# Revit family: 0010232
name_source: partatom
category: Lighting Fixtures
revit_build: Autodesk Revit 2017 (Build: 20190507_1515(x64)
units: mm (PartAtom-declared; Revit-internal decimal feet)

## family parameters
Cut with Voids When Loaded = No
Host = Face
Light Source = Yes
OmniClass Number = 23.80.70.00
OmniClass Title = Lighting
Part Type = Normal
Room Calculation Point = No
Round Connector Dimension = Use Diameter
Shared = No

## types (60) — shared parameters
Assembly Code = D5020200
AssetType = Fixed
BODY_SYL = 36 mm  [stored 0.11811 ft]
BRACKET_HEIGHT_SYL = 9 mm
CHAMFER_SYL = 19 mm
ClassificationName = Uniclass2015
ClassificationValue = EF_70_80
Color Filter = 16777215
DIF_HEIGHT_SYL = 24 mm
DIF_WIDHT_SYL = 35 mm  [stored 0.114829 ft]
Default Elevation = 1219 mm
Dimming Lamp Color Temperature Shift = <None>
DocumentationLiterature = http://www.sylvania-lighting.com
ElectricShockClassification = Class I
Emit Shape Visible in Rendering = No
Emit from Circle Diameter = 610 mm
IfcExportAs = IfcLightFixtureType
IfcExportType = IfcLightFixtureType
ImpactProtectionIndex = IK08
IngressProtection = IP66
Keynote = 16500
LEGHT_1200-_SYL = -600 mm
LEGHT_1200_SYL = 600 mm
LEGHT_1500-_SYL = -750 mm  [stored -2.46063 ft]
LEGHT_1500_SYL = 750 mm  [stored 2.46063 ft]
LEGHT_650-_SYL = -325 mm  [stored -1.06627 ft]
LENGHT_650_SYL = 325 mm  [stored 1.06627 ft]
Lamp = LED
LampColourRenderingIndex = 80
LampsType = LED
MID_WIDTH_SYL = 36 mm  [stored 0.11811 ft]
Manufacturer = Feilo Sylvania
ManufacturerName = Feilo Sylvania
Material = pc polycarbonate housing, pc polycarbonate diffuser
Material_1_SYL = Default
Material_2_SYL = <By Category>
Material_3_SYL = <By Category>
Material_4_SYL = <By Category>
NominalDepth = 87 mm  [stored 0.285433 ft]
NominalHeight = 80 mm  [stored 0.262467 ft]
TOP_WIDTH_SYL = 34 mm
Tilt Angle = -90.00°
Type Image = <None>
URL = http://www.sylvania-lighting.com
Voltage = 0 V
WIDTH_SYL = 45 mm
zero-valued in all types: Cost

## per-type parameters (varying)
- 0010278 RESISTO 1500 HE IP66 8300LM 840: Apparent Load=54 VA; BRACKET_DIST_SYL=594 mm; BRACKET_WIDTH_SYL=550 mm; Description=Resisto, integrated LED weatherproof luminaire, with UV stabilized flat diffuser designed to achieve uniform lit appearance, optimise light output and to reduce glare. 301 stainless steel diffuser clips and fixing brackets for surface mounting. Polycarbonate housing and diffuser - no yellow discolouration over time. 8300lm; 54W; 154lm/W; 4000K; SDCM<3; non dimmable; CRI80; IP66; IK08; Class I; 69,000hrs (L80B20) lifespan; 1500mm x 89mm x 88mm; D-mark.; L0650_SYL=No; L1200_SYL=No; L1500_SYL=Yes; LENGHT-_CHAMFER_SYL=-750 mm  [stored -2.46063 ft]; LENGHT-_SYL=-742 mm  [stored -2.43438 ft]; LENGHT_CHAMFER_SYL=750 mm  [stored 2.46063 ft]; LENGHT_SYL=742 mm  [stored 2.43438 ft]; LampColourTemperature=4000 K; LampMacAdamStep=3; LampNominalLuminous=8300 lm; LuminousEfficacy=154 lm/W; Model=Resisto 1500 HE IP66 8300lm 840; ModelNumber=0010278; ModelReference=Resisto 1500 HE IP66 8300lm 840; Name=Resisto 1500 HE IP66 8300lm 840; NominalLength=1500 mm  [stored 4.92126 ft]; Photometric Web File=0010278.ies; PowerConsumption=54 W; PowerFactor=0.95; TypeName=Resisto 1500 HE IP66 8300lm 840; Weight=1.95 kg
- 0010274 RESISTO 1500 HE IP66 DALI 7100LM 840: Apparent Load=46 VA; BRACKET_DIST_SYL=594 mm; BRACKET_WIDTH_SYL=550 mm; Description=Resisto, integrated LED weatherproof luminaire, with UV stabilized flat diffuser designed to achieve uniform lit appearance, optimise light output and to reduce glare. 301 stainless steel diffuser clips and fixing brackets for surface mounting. Polycarbonate housing and diffuser - no yellow discolouration over time. 7100lm; 46W; 154lm/W; 4000K; SDCM<3; DALI dimmable; CRI80; IP66; IK08; Class I; 69,000hrs (L80B20) lifespan; 1500mm x 89mm x 88mm; D-mark.; L0650_SYL=No; L1200_SYL=No; L1500_SYL=Yes; LENGHT-_CHAMFER_SYL=-750 mm  [stored -2.46063 ft]; LENGHT-_SYL=-742 mm  [stored -2.43438 ft]; LENGHT_CHAMFER_SYL=750 mm  [stored 2.46063 ft]; LENGHT_SYL=742 mm  [stored 2.43438 ft]; LampColourTemperature=4000 K; LampMacAdamStep=3; LampNominalLuminous=7100 lm; LuminousEfficacy=154 lm/W; Model=Resisto 1500 HE IP66 DALI 7100lm 840; ModelNumber=0010274; ModelReference=Resisto 1500 HE IP66 DALI 7100lm 840; Name=Resisto 1500 HE IP66 DALI 7100lm 840; NominalLength=1500 mm  [stored 4.92126 ft]; Photometric Web File=0010274.ies; PowerConsumption=46 W; PowerFactor=0.98; TypeName=Resisto 1500 HE IP66 DALI 7100lm 840; Weight=2.01 kg
- 0010273 RESISTO 1500 HE IP66 DALI 4000LM 840: Apparent Load=25 VA; BRACKET_DIST_SYL=594 mm; BRACKET_WIDTH_SYL=550 mm; Description=Resisto, integrated LED weatherproof luminaire, with UV stabilized flat diffuser designed to achieve uniform lit appearance, optimise light output and to reduce glare. 301 stainless steel diffuser clips and fixing brackets for surface mounting. Polycarbonate housing and diffuser - no yellow discolouration over time. 4000lm; 25W; 160lm/W; 4000K; SDCM<3; DALI dimmable; CRI80; IP66; IK08; Class I; 69,000hrs (L80B20) lifespan; 1500mm x 89mm x 88mm; D-mark.; L0650_SYL=No; L1200_SYL=No; L1500_SYL=Yes; LENGHT-_CHAMFER_SYL=-750 mm  [stored -2.46063 ft]; LENGHT-_SYL=-742 mm  [stored -2.43438 ft]; LENGHT_CHAMFER_SYL=750 mm  [stored 2.46063 ft]; LENGHT_SYL=742 mm  [stored 2.43438 ft]; LampColourTemperature=4000 K; LampMacAdamStep=3; LampNominalLuminous=4000 lm; LuminousEfficacy=160 lm/W; Model=Resisto 1500 HE IP66 DALI 4000lm 840; ModelNumber=0010273; ModelReference=Resisto 1500 HE IP66 DALI 4000lm 840; Name=Resisto 1500 HE IP66 DALI 4000lm 840; NominalLength=1500 mm  [stored 4.92126 ft]; Photometric Web File=0010273.ies; PowerConsumption=25 W; PowerFactor=0.98; TypeName=Resisto 1500 HE IP66 DALI 4000lm 840; Weight=1.95 kg
- 0010272 RESISTO 1500 HE IP66 7100LM 840 EM: Apparent Load=50 VA; BRACKET_DIST_SYL=594 mm; BRACKET_WIDTH_SYL=550 mm; Description=Resisto, integrated LED weatherproof luminaire, with UV stabilized flat diffuser designed to achieve uniform lit appearance, optimise light output and to reduce glare. 301 stainless steel diffuser clips and fixing brackets for surface mounting. Polycarbonate housing and diffuser - no yellow discolouration over time. 7100lm; 50W; 142lm/W; 4000K; SDCM<3; non dimmable; CRI80; IP66; IK08; Class I; 69,000hrs (L80B20) lifespan; 1500mm x 89mm x 88mm; D-mark; 3-hour maintained emergency batteries.; L0650_SYL=No; L1200_SYL=No; L1500_SYL=Yes; LENGHT-_CHAMFER_SYL=-750 mm  [stored -2.46063 ft]; LENGHT-_SYL=-742 mm  [stored -2.43438 ft]; LENGHT_CHAMFER_SYL=750 mm  [stored 2.46063 ft]; LENGHT_SYL=742 mm  [stored 2.43438 ft]; LampColourTemperature=4000 K; LampMacAdamStep=3; LampNominalLuminous=7100 lm; LuminousEfficacy=142 lm/W; Model=Resisto 1500 HE IP66 7100lm 840 EM; ModelNumber=0010272; ModelReference=Resisto 1500 HE IP66 7100lm 840 EM; Name=Resisto 1500 HE IP66 7100lm 840 EM; NominalLength=1500 mm  [stored 4.92126 ft]; Photometric Web File=0010272.ies; PowerConsumption=50 W; PowerFactor=0.95; TypeName=Resisto 1500 HE IP66 7100lm 840 EM; Weight=2.58 kg
- 0010271 RESISTO 1500 HE IP66 4000LM 840 EM: Apparent Load=29 VA; BRACKET_DIST_SYL=594 mm; BRACKET_WIDTH_SYL=550 mm; Description=Resisto, integrated LED weatherproof luminaire, with UV stabilized flat diffuser designed to achieve uniform lit appearance, optimise light output and to reduce glare. 301 stainless steel diffuser clips and fixing brackets for surface mounting. Polycarbonate housing and diffuser - no yellow discolouration over time. 4000lm; 29W; 138lm/W; 4000K; SDCM<3; non dimmable; CRI80; IP66; IK08; Class I; 69,000hrs (L80B20) lifespan; 1500mm x 89mm x 88mm; D-mark; 3-hour maintained emergency batteries.; L0650_SYL=No; L1200_SYL=No; L1500_SYL=Yes; LENGHT-_CHAMFER_SYL=-750 mm  [stored -2.46063 ft]; LENGHT-_SYL=-742 mm  [stored -2.43438 ft]; LENGHT_CHAMFER_SYL=750 mm  [stored 2.46063 ft]; LENGHT_SYL=742 mm  [stored 2.43438 ft]; LampColourTemperature=4000 K; LampMacAdamStep=3; LampNominalLuminous=4000 lm; LuminousEfficacy=138 lm/W; Model=Resisto 1500 HE IP66 4000lm 840 EM; ModelNumber=0010271; ModelReference=Resisto 1500 HE IP66 4000lm 840 EM; Name=Resisto 1500 HE IP66 4000lm 840 EM; NominalLength=1500 mm  [stored 4.92126 ft]; Photometric Web File=0010271.ies; PowerConsumption=29 W; PowerFactor=0.95; TypeName=Resisto 1500 HE IP66 4000lm 840 EM; Weight=2.51 kg
- 0010269 RESISTO 1500 HE IP66 7100LM 840: Apparent Load=46 VA; BRACKET_DIST_SYL=594 mm; BRACKET_WIDTH_SYL=550 mm; Description=Resisto, integrated LED weatherproof luminaire, with UV stabilized flat diffuser designed to achieve uniform lit appearance, optimise light output and to reduce glare. 301 stainless steel diffuser clips and fixing brackets for surface mounting. Polycarbonate housing and diffuser - no yellow discolouration over time. 7100lm; 46W; 154lm/W; 4000K; SDCM<3; non dimmable; CRI80; IP66; IK08; Class I; 69,000hrs (L80B20) lifespan; 1500mm x 89mm x 88mm; D-mark.; L0650_SYL=No; L1200_SYL=No; L1500_SYL=Yes; LENGHT-_CHAMFER_SYL=-750 mm  [stored -2.46063 ft]; LENGHT-_SYL=-742 mm  [stored -2.43438 ft]; LENGHT_CHAMFER_SYL=750 mm  [stored 2.46063 ft]; LENGHT_SYL=742 mm  [stored 2.43438 ft]; LampColourTemperature=4000 K; LampMacAdamStep=3; LampNominalLuminous=7100 lm; LuminousEfficacy=154 lm/W; Model=Resisto  1500 HE IP66 7100lm 840; ModelNumber=0010269; ModelReference=Resisto  1500 HE IP66 7100lm 840; Name=Resisto  1500 HE IP66 7100lm 840; NominalLength=1500 mm  [stored 4.92126 ft]; Photometric Web File=0010269.ies; PowerConsumption=46 W; PowerFactor=0.95; TypeName=Resisto  1500 HE IP66 7100lm 840; Weight=1.95 kg
- 0010268 RESISTO 1500 HE IP66 4000LM 840: Apparent Load=25 VA; BRACKET_DIST_SYL=594 mm; BRACKET_WIDTH_SYL=550 mm; Description=Resisto, integrated LED weatherproof luminaire, with UV stabilized flat diffuser designed to achieve uniform lit appearance, optimise light output and to reduce glare. 301 stainless steel diffuser clips and fixing brackets for surface mounting. Polycarbonate housing and diffuser - no yellow discolouration over time. 4000lm; 25W; 160lm/W; 4000K; SDCM<3; non dimmable; CRI80; IP66; IK08; Class I; 69,000hrs (L80B20) lifespan; 1500mm x 89mm x 88mm; D-mark.; L0650_SYL=No; L1200_SYL=No; L1500_SYL=Yes; LENGHT-_CHAMFER_SYL=-750 mm  [stored -2.46063 ft]; LENGHT-_SYL=-742 mm  [stored -2.43438 ft]; LENGHT_CHAMFER_SYL=750 mm  [stored 2.46063 ft]; LENGHT_SYL=742 mm  [stored 2.43438 ft]; LampColourTemperature=4000 K; LampMacAdamStep=3; LampNominalLuminous=4000 lm; LuminousEfficacy=160 lm/W; Model=Resisto  1500 HE IP66 4000lm 840; ModelNumber=0010268; ModelReference=Resisto  1500 HE IP66 4000lm 840; Name=Resisto  1500 HE IP66 4000lm 840; NominalLength=1500 mm  [stored 4.92126 ft]; Photometric Web File=0010268.ies; PowerConsumption=25 W; PowerFactor=0.95; TypeName=Resisto  1500 HE IP66 4000lm 840; Weight=1.87 kg
- 0010261 RESISTO 1500 IP66 DALI 8300LM 840: Apparent Load=61 VA; BRACKET_DIST_SYL=594 mm; BRACKET_WIDTH_SYL=550 mm; Description=Resisto, integrated LED weatherproof luminaire, with UV stabilized flat diffuser designed to achieve uniform lit appearance, optimise light output and to reduce glare. 301 stainless steel diffuser clips and fixing brackets for surface mounting. Polycarbonate housing and diffuser - no yellow discolouration over time. 8300lm; 61W; 136lm/W; 4000K; SDCM<5; DALI dimmable; CRI80; IP66; IK08; Class I; 69,000hrs (L80B20) lifespan; 1500mm x 89mm x 88mm; D-mark.; L0650_SYL=No; L1200_SYL=No; L1500_SYL=Yes; LENGHT-_CHAMFER_SYL=-750 mm  [stored -2.46063 ft]; LENGHT-_SYL=-742 mm  [stored -2.43438 ft]; LENGHT_CHAMFER_SYL=750 mm  [stored 2.46063 ft]; LENGHT_SYL=742 mm  [stored 2.43438 ft]; LampColourTemperature=4000 K; LampMacAdamStep=5; LampNominalLuminous=8300 lm; LuminousEfficacy=136 lm/W; Model=Resisto  1500 IP66 DALI 8300lm 840; ModelNumber=0010261; ModelReference=Resisto  1500 IP66 DALI 8300lm 840; Name=Resisto  1500 IP66 DALI 8300lm 840; NominalLength=1500 mm  [stored 4.92126 ft]; Photometric Web File=0010261.ies; PowerConsumption=61 W; PowerFactor=0.99; TypeName=Resisto  1500 IP66 DALI 8300lm 840; Weight=2.01 kg
- 0010260 RESISTO 1500 IP66 DALI 7100LM 840: Apparent Load=52 VA; BRACKET_DIST_SYL=594 mm; BRACKET_WIDTH_SYL=550 mm; Description=Resisto, integrated LED weatherproof luminaire, with UV stabilized flat diffuser designed to achieve uniform lit appearance, optimise light output and to reduce glare. 301 stainless steel diffuser clips and fixing brackets for surface mounting. Polycarbonate housing and diffuser - no yellow discolouration over time. 7100lm; 52W; 137lm/W; 4000K; SDCM<5; DALI dimmable; CRI80; IP66; IK08; Class I; 69,000hrs (L80B20) lifespan; 1500mm x 89mm x 88mm; D-mark.; L0650_SYL=No; L1200_SYL=No; L1500_SYL=Yes; LENGHT-_CHAMFER_SYL=-750 mm  [stored -2.46063 ft]; LENGHT-_SYL=-742 mm  [stored -2.43438 ft]; LENGHT_CHAMFER_SYL=750 mm  [stored 2.46063 ft]; LENGHT_SYL=742 mm  [stored 2.43438 ft]; LampColourTemperature=4000 K; LampMacAdamStep=5; LampNominalLuminous=7100 lm; LuminousEfficacy=137 lm/W; Model=Resisto  1500 IP66 DALI 7100lm 840; ModelNumber=0010260; ModelReference=Resisto  1500 IP66 DALI 7100lm 840; Name=Resisto  1500 IP66 DALI 7100lm 840; NominalLength=1500 mm  [stored 4.92126 ft]; Photometric Web File=0010260.ies; PowerConsumption=52 W; PowerFactor=0.99; TypeName=Resisto  1500 IP66 DALI 7100lm 840; Weight=2.01 kg
- 0010259 RESISTO 1500 IP66 DALI 4000LM 840: Apparent Load=30 VA; BRACKET_DIST_SYL=594 mm; BRACKET_WIDTH_SYL=550 mm; Description=Resisto, integrated LED weatherproof luminaire, with UV stabilized flat diffuser designed to achieve uniform lit appearance, optimise light output and to reduce glare. 301 stainless steel diffuser clips and fixing brackets for surface mounting. Polycarbonate housing and diffuser - no yellow discolouration over time. 4000lm; 30W; 133lm/W; 4000K; SDCM<5; DALI dimmable; CRI80; IP66; IK08; Class I; 69,000hrs (L80B20) lifespan; 1500mm x 89mm x 88mm; D-mark.; L0650_SYL=No; L1200_SYL=No; L1500_SYL=Yes; LENGHT-_CHAMFER_SYL=-750 mm  [stored -2.46063 ft]; LENGHT-_SYL=-742 mm  [stored -2.43438 ft]; LENGHT_CHAMFER_SYL=750 mm  [stored 2.46063 ft]; LENGHT_SYL=742 mm  [stored 2.43438 ft]; LampColourTemperature=4000 K; LampMacAdamStep=5; LampNominalLuminous=4000 lm; LuminousEfficacy=133 lm/W; Model=Resisto  1500 IP66 DALI 4000lm 840; ModelNumber=0010259; ModelReference=Resisto  1500 IP66 DALI 4000lm 840; Name=Resisto  1500 IP66 DALI 4000lm 840; NominalLength=1500 mm  [stored 4.92126 ft]; Photometric Web File=0010259.ies; PowerConsumption=30 W; PowerFactor=0.98; TypeName=Resisto  1500 IP66 DALI 4000lm 840; Weight=1.95 kg
- 0010258 RESISTO 1500 IP66 MWCOR 7100LM 840: Apparent Load=52 VA; BRACKET_DIST_SYL=594 mm; BRACKET_WIDTH_SYL=550 mm; Description=Resisto, integrated LED weatherproof luminaire, with UV stabilized flat diffuser designed to achieve uniform lit appearance, optimise light output and to reduce glare. 301 stainless steel diffuser clips and fixing brackets for surface mounting. Polycarbonate housing and diffuser - no yellow discolouration over time. 7100lm; 52W; 137lm/W; 4000K; SDCM<5; non dimmable; CRI80; IP66; IK08; Class I; 69,000hrs (L80B20) lifespan; 1500mm x 89mm x 88mm; D-mark; corridor function with microwave presence sensor.; L0650_SYL=No; L1200_SYL=No; L1500_SYL=Yes; LENGHT-_CHAMFER_SYL=-750 mm  [stored -2.46063 ft]; LENGHT-_SYL=-742 mm  [stored -2.43438 ft]; LENGHT_CHAMFER_SYL=750 mm  [stored 2.46063 ft]; LENGHT_SYL=742 mm  [stored 2.43438 ft]; LampColourTemperature=4000 K; LampMacAdamStep=5; LampNominalLuminous=7100 lm; LuminousEfficacy=137 lm/W; Model=Resisto  1500 IP66 MWcor 7100lm 840; ModelNumber=0010258; ModelReference=Resisto  1500 IP66 MWcor 7100lm 840; Name=Resisto  1500 IP66 MWcor 7100lm 840; NominalLength=1500 mm  [stored 4.92126 ft]; Photometric Web File=0010258.ies; PowerConsumption=52 W; PowerFactor=0.99; TypeName=Resisto  1500 IP66 MWcor 7100lm 840; Weight=2.06 kg
- 0010257 RESISTO 1500 IP66 MWCOR 4000LM 840: Apparent Load=30 VA; BRACKET_DIST_SYL=594 mm; BRACKET_WIDTH_SYL=550 mm; Description=Resisto, integrated LED weatherproof luminaire, with UV stabilized flat diffuser designed to achieve uniform lit appearance, optimise light output and to reduce glare. 301 stainless steel diffuser clips and fixing brackets for surface mounting. Polycarbonate housing and diffuser - no yellow discolouration over time. 4000lm; 30W; 133lm/W; 4000K; SDCM<5; non dimmable; CRI80; IP66; IK08; Class I; 69,000hrs (L80B20) lifespan; 1500mm x 89mm x 88mm; D-mark; corridor function with microwave presence sensor.; L0650_SYL=No; L1200_SYL=No; L1500_SYL=Yes; LENGHT-_CHAMFER_SYL=-750 mm  [stored -2.46063 ft]; LENGHT-_SYL=-742 mm  [stored -2.43438 ft]; LENGHT_CHAMFER_SYL=750 mm  [stored 2.46063 ft]; LENGHT_SYL=742 mm  [stored 2.43438 ft]; LampColourTemperature=4000 K; LampMacAdamStep=5; LampNominalLuminous=4000 lm; LuminousEfficacy=133 lm/W; Model=Resisto  1500 IP66 MWcor 4000lm 840; ModelNumber=0010257; ModelReference=Resisto  1500 IP66 MWcor 4000lm 840; Name=Resisto  1500 IP66 MWcor 4000lm 840; NominalLength=1500 mm  [stored 4.92126 ft]; Photometric Web File=0010257.ies; PowerConsumption=30 W; PowerFactor=0.98; TypeName=Resisto  1500 IP66 MWcor 4000lm 840; Weight=2.0 kg
- 0010256 RESISTO 1500 IP66 MW 7100LM 840: Apparent Load=52 VA; BRACKET_DIST_SYL=594 mm; BRACKET_WIDTH_SYL=550 mm; Description=Resisto, integrated LED weatherproof luminaire, with UV stabilized flat diffuser designed to achieve uniform lit appearance, optimise light output and to reduce glare. 301 stainless steel diffuser clips and fixing brackets for surface mounting. Polycarbonate housing and diffuser - no yellow discolouration over time. 7100lm; 52W; 137lm/W; 4000K; SDCM<5; non dimmable; CRI80; IP66; IK08; Class I; 69,000hrs (L80B20) lifespan; 1500mm x 89mm x 88mm; D-mark; MW On/Off.; L0650_SYL=No; L1200_SYL=No; L1500_SYL=Yes; LENGHT-_CHAMFER_SYL=-750 mm  [stored -2.46063 ft]; LENGHT-_SYL=-742 mm  [stored -2.43438 ft]; LENGHT_CHAMFER_SYL=750 mm  [stored 2.46063 ft]; LENGHT_SYL=742 mm  [stored 2.43438 ft]; LampColourTemperature=4000 K; LampMacAdamStep=5; LampNominalLuminous=7100 lm; LuminousEfficacy=137 lm/W; Model=Resisto  1500 IP66 MW 7100lm 840; ModelNumber=0010256; ModelReference=Resisto  1500 IP66 MW 7100lm 840; Name=Resisto  1500 IP66 MW 7100lm 840; NominalLength=1500 mm  [stored 4.92126 ft]; Photometric Web File=0010256.ies; PowerConsumption=52 W; PowerFactor=0.95; TypeName=Resisto  1500 IP66 MW 7100lm 840; Weight=2.0 kg
- 0010255 RESISTO 1500 IP66 MW 4000LM 840: Apparent Load=30 VA; BRACKET_DIST_SYL=594 mm; BRACKET_WIDTH_SYL=550 mm; Description=Resisto, integrated LED weatherproof luminaire, with UV stabilized flat diffuser designed to achieve uniform lit appearance, optimise light output and to reduce glare. 301 stainless steel diffuser clips and fixing brackets for surface mounting. Polycarbonate housing and diffuser - no yellow discolouration over time. 4000lm; 30W; 133lm/W; 4000K; SDCM<5; non dimmable; CRI80; IP66; IK08; Class I; 69,000hrs (L80B20) lifespan; 1500mm x 89mm x 88mm; D-mark; MW On/Off.; L0650_SYL=No; L1200_SYL=No; L1500_SYL=Yes; LENGHT-_CHAMFER_SYL=-750 mm  [stored -2.46063 ft]; LENGHT-_SYL=-742 mm  [stored -2.43438 ft]; LENGHT_CHAMFER_SYL=750 mm  [stored 2.46063 ft]; LENGHT_SYL=742 mm  [stored 2.43438 ft]; LampColourTemperature=4000 K; LampMacAdamStep=5; LampNominalLuminous=4000 lm; LuminousEfficacy=133 lm/W; Model=Resisto  1500 IP66 MW 4000lm 840; ModelNumber=0010255; ModelReference=Resisto  1500 IP66 MW 4000lm 840; Name=Resisto  1500 IP66 MW 4000lm 840; NominalLength=1500 mm  [stored 4.92126 ft]; Photometric Web File=0010255.ies; PowerConsumption=30 W; PowerFactor=0.95; TypeName=Resisto  1500 IP66 MW 4000lm 840; Weight=1.92 kg
- 0010254 RESISTO 1500 IP66 7100LM 840 EM: Apparent Load=56 VA; BRACKET_DIST_SYL=594 mm; BRACKET_WIDTH_SYL=550 mm; Description=Resisto, integrated LED weatherproof luminaire, with UV stabilized flat diffuser designed to achieve uniform lit appearance, optimise light output and to reduce glare. 301 stainless steel diffuser clips and fixing brackets for surface mounting. Polycarbonate housing and diffuser - no yellow discolouration over time. 7100lm; 56W; 127lm/W; 4000K; SDCM<5; non dimmable; CRI80; IP66; IK08; Class I; 69,000hrs (L80B20) lifespan; 1500mm x 89mm x 88mm; D-mark; 3-hour maintained emergency batteries.; L0650_SYL=No; L1200_SYL=No; L1500_SYL=Yes; LENGHT-_CHAMFER_SYL=-750 mm  [stored -2.46063 ft]; LENGHT-_SYL=-742 mm  [stored -2.43438 ft]; LENGHT_CHAMFER_SYL=750 mm  [stored 2.46063 ft]; LENGHT_SYL=742 mm  [stored 2.43438 ft]; LampColourTemperature=4000 K; LampMacAdamStep=5; LampNominalLuminous=7100 lm; LuminousEfficacy=127 lm/W; Model=Resisto  1500 IP66 7100lm 840 EM; ModelNumber=0010254; ModelReference=Resisto  1500 IP66 7100lm 840 EM; Name=Resisto  1500 IP66 7100lm 840 EM; NominalLength=1500 mm  [stored 4.92126 ft]; Photometric Web File=0010254.ies; PowerConsumption=56 W; PowerFactor=0.95; TypeName=Resisto  1500 IP66 7100lm 840 EM; Weight=2.59 kg
- 0010253 RESISTO 1500 IP66 4000LM 840 EM: Apparent Load=34 VA; BRACKET_DIST_SYL=594 mm; BRACKET_WIDTH_SYL=550 mm; Description=Resisto, integrated LED weatherproof luminaire, with UV stabilized flat diffuser designed to achieve uniform lit appearance, optimise light output and to reduce glare. 301 stainless steel diffuser clips and fixing brackets for surface mounting. Polycarbonate housing and diffuser - no yellow discolouration over time. 4000lm; 34W; 118lm/W; 4000K; SDCM<5; non dimmable; CRI80; IP66; IK08; Class I; 69,000hrs (L80B20) lifespan; 1500mm x 89mm x 88mm; D-mark; 3-hour maintained emergency batteries.; L0650_SYL=No; L1200_SYL=No; L1500_SYL=Yes; LENGHT-_CHAMFER_SYL=-750 mm  [stored -2.46063 ft]; LENGHT-_SYL=-742 mm  [stored -2.43438 ft]; LENGHT_CHAMFER_SYL=750 mm  [stored 2.46063 ft]; LENGHT_SYL=742 mm  [stored 2.43438 ft]; LampColourTemperature=4000 K; LampMacAdamStep=5; LampNominalLuminous=4000 lm; LuminousEfficacy=118 lm/W; Model=Resisto  1500 IP66 4000lm 840 EM; ModelNumber=0010253; ModelReference=Resisto  1500 IP66 4000lm 840 EM; Name=Resisto  1500 IP66 4000lm 840 EM; NominalLength=1500 mm  [stored 4.92126 ft]; Photometric Web File=0010253.ies; PowerConsumption=34 W; PowerFactor=0.95; TypeName=Resisto  1500 IP66 4000lm 840 EM; Weight=2.5 kg
- 0010252 RESISTO 1500 IP66 7100LM 840 5XTH: Apparent Load=52 VA; BRACKET_DIST_SYL=594 mm; BRACKET_WIDTH_SYL=550 mm; Description=Resisto, integrated LED weatherproof luminaire, with UV stabilized flat diffuser designed to achieve uniform lit appearance, optimise light output and to reduce glare. 301 stainless steel diffuser clips and fixing brackets for surface mounting. Polycarbonate housing and diffuser - no yellow discolouration over time. 7100lm; 52W; 137lm/W; 4000K; SDCM<5; non dimmable; CRI80; IP66; IK08; Class I; 69,000hrs (L80B20) lifespan; 1500mm x 89mm x 88mm; D-mark; through wiring.; L0650_SYL=No; L1200_SYL=No; L1500_SYL=Yes; LENGHT-_CHAMFER_SYL=-750 mm  [stored -2.46063 ft]; LENGHT-_SYL=-742 mm  [stored -2.43438 ft]; LENGHT_CHAMFER_SYL=750 mm  [stored 2.46063 ft]; LENGHT_SYL=742 mm  [stored 2.43438 ft]; LampColourTemperature=4000 K; LampMacAdamStep=5; LampNominalLuminous=7100 lm; LuminousEfficacy=137 lm/W; Model=Resisto 1500 IP66 7100lm 840 5xTH; ModelNumber=0010252; ModelReference=Resisto 1500 IP66 7100lm 840 5xTH; Name=Resisto 1500 IP66 7100lm 840 5xTH; NominalLength=1500 mm  [stored 4.92126 ft]; Photometric Web File=0010252.ies; PowerConsumption=52 W; PowerFactor=0.95; TypeName=Resisto 1500 IP66 7100lm 840 5xTH; Weight=2.18 kg
- 0010251 RESISTO 1500 IP66 4000LM 840 5XTH: Apparent Load=30 VA; BRACKET_DIST_SYL=594 mm; BRACKET_WIDTH_SYL=550 mm; Description=Resisto, integrated LED weatherproof luminaire, with UV stabilized flat diffuser designed to achieve uniform lit appearance, optimise light output and to reduce glare. 301 stainless steel diffuser clips and fixing brackets for surface mounting. Polycarbonate housing and diffuser - no yellow discolouration over time. 4000lm; 30W; 133lm/W; 4000K; SDCM<5; non dimmable; CRI80; IP66; IK08; Class I; 69,000hrs (L80B20) lifespan; 1500mm x 89mm x 88mm; D-mark; through wiring.; L0650_SYL=No; L1200_SYL=No; L1500_SYL=Yes; LENGHT-_CHAMFER_SYL=-750 mm  [stored -2.46063 ft]; LENGHT-_SYL=-742 mm  [stored -2.43438 ft]; LENGHT_CHAMFER_SYL=750 mm  [stored 2.46063 ft]; LENGHT_SYL=742 mm  [stored 2.43438 ft]; LampColourTemperature=4000 K; LampMacAdamStep=5; LampNominalLuminous=4000 lm; LuminousEfficacy=133 lm/W; Model=Resisto 1500 IP66 4000lm 840 5xTH; ModelNumber=0010251; ModelReference=Resisto 1500 IP66 4000lm 840 5xTH; Name=Resisto 1500 IP66 4000lm 840 5xTH; NominalLength=1500 mm  [stored 4.92126 ft]; Photometric Web File=0010251.ies; PowerConsumption=30 W; PowerFactor=0.95; TypeName=Resisto 1500 IP66 4000lm 840 5xTH; Weight=2.1 kg
- 0010250 RESISTO 1500 IP66 7100LM 840 QC: Apparent Load=52 VA; BRACKET_DIST_SYL=594 mm; BRACKET_WIDTH_SYL=550 mm; Description=Resisto, integrated LED weatherproof luminaire, with UV stabilized flat diffuser designed to achieve uniform lit appearance, optimise light output and to reduce glare. 301 stainless steel diffuser clips and fixing brackets for surface mounting. Polycarbonate housing and diffuser - no yellow discolouration over time. 7100lm; 52W; 137lm/W; 4000K; SDCM<5; non dimmable; CRI80; IP66; IK08; Class I; 69,000hrs (L80B20) lifespan; 1500mm x 89mm x 88mm; D-mark; assembled with quick connector.; L0650_SYL=No; L1200_SYL=No; L1500_SYL=Yes; LENGHT-_CHAMFER_SYL=-750 mm  [stored -2.46063 ft]; LENGHT-_SYL=-742 mm  [stored -2.43438 ft]; LENGHT_CHAMFER_SYL=750 mm  [stored 2.46063 ft]; LENGHT_SYL=742 mm  [stored 2.43438 ft]; LampColourTemperature=4000 K; LampMacAdamStep=5; LampNominalLuminous=7100 lm; LuminousEfficacy=137 lm/W; Model=Resisto  1500 IP66 7100lm 840 QC; ModelNumber=0010250; ModelReference=Resisto  1500 IP66 7100lm 840 QC; Name=Resisto  1500 IP66 7100lm 840 QC; NominalLength=1512 mm  [stored 4.96063 ft]; Photometric Web File=0010250.ies; PowerConsumption=52 W; PowerFactor=0.95; TypeName=Resisto  1500 IP66 7100lm 840 QC; Weight=2.02 kg
- 0010249 RESISTO 1500 IP66 4000LM 840 QC: Apparent Load=30 VA; BRACKET_DIST_SYL=594 mm; BRACKET_WIDTH_SYL=550 mm; Description=Resisto, integrated LED weatherproof luminaire, with UV stabilized flat diffuser designed to achieve uniform lit appearance, optimise light output and to reduce glare. 301 stainless steel diffuser clips and fixing brackets for surface mounting. Polycarbonate housing and diffuser - no yellow discolouration over time. 4000lm; 30W; 133lm/W; 4000K; SDCM<5; non dimmable; CRI80; IP66; IK08; Class I; 69,000hrs (L80B20) lifespan; 1500mm x 89mm x 88mm; D-mark; assembled with quick connector.; L0650_SYL=No; L1200_SYL=No; L1500_SYL=Yes; LENGHT-_CHAMFER_SYL=-750 mm  [stored -2.46063 ft]; LENGHT-_SYL=-742 mm  [stored -2.43438 ft]; LENGHT_CHAMFER_SYL=750 mm  [stored 2.46063 ft]; LENGHT_SYL=742 mm  [stored 2.43438 ft]; LampColourTemperature=4000 K; LampMacAdamStep=5; LampNominalLuminous=4000 lm; LuminousEfficacy=133 lm/W; Model=Resisto  1500 IP66 4000lm 840 QC; ModelNumber=0010249; ModelReference=Resisto  1500 IP66 4000lm 840 QC; Name=Resisto  1500 IP66 4000lm 840 QC; NominalLength=1512 mm  [stored 4.96063 ft]; Photometric Web File=0010249.ies; PowerConsumption=30 W; PowerFactor=0.95; TypeName=Resisto  1500 IP66 4000lm 840 QC; Weight=1.94 kg
- 0010248 RESISTO 1500 IP66 8300LM 865: Apparent Load=61 VA; BRACKET_DIST_SYL=594 mm; BRACKET_WIDTH_SYL=550 mm; Description=Resisto, integrated LED weatherproof luminaire, with UV stabilized flat diffuser designed to achieve uniform lit appearance, optimise light output and to reduce glare. 301 stainless steel diffuser clips and fixing brackets for surface mounting. Polycarbonate housing and diffuser - no yellow discolouration over time. 8300lm; 61W; 136lm/W; 6500K; SDCM<5; non dimmable; CRI80; IP66; IK08; Class I; 69,000hrs (L80B20) lifespan; 1500mm x 89mm x 88mm; D-mark.; L0650_SYL=No; L1200_SYL=No; L1500_SYL=Yes; LENGHT-_CHAMFER_SYL=-750 mm  [stored -2.46063 ft]; LENGHT-_SYL=-742 mm  [stored -2.43438 ft]; LENGHT_CHAMFER_SYL=750 mm  [stored 2.46063 ft]; LENGHT_SYL=742 mm  [stored 2.43438 ft]; LampColourTemperature=6500 K; LampMacAdamStep=5; LampNominalLuminous=8300 lm; LuminousEfficacy=136 lm/W; Model=Resisto  1500 IP66 8300lm 865; ModelNumber=0010248; ModelReference=Resisto  1500 IP66 8300lm 865; Name=Resisto  1500 IP66 8300lm 865; NominalLength=1500 mm  [stored 4.92126 ft]; Photometric Web File=0010248.ies; PowerConsumption=61 W; PowerFactor=0.95; TypeName=Resisto  1500 IP66 8300lm 865; Weight=1.95 kg
- 0010247 RESISTO 1500 IP66 7100LM 865: Apparent Load=52 VA; BRACKET_DIST_SYL=594 mm; BRACKET_WIDTH_SYL=550 mm; Description=Resisto, integrated LED weatherproof luminaire, with UV stabilized flat diffuser designed to achieve uniform lit appearance, optimise light output and to reduce glare. 301 stainless steel diffuser clips and fixing brackets for surface mounting. Polycarbonate housing and diffuser - no yellow discolouration over time. 7100lm; 52W; 137lm/W; 6500K; SDCM<5; non dimmable; CRI80; IP66; IK08; Class I; 69,000hrs (L80B20) lifespan; 1500mm x 89mm x 88mm; D-mark.; L0650_SYL=No; L1200_SYL=No; L1500_SYL=Yes; LENGHT-_CHAMFER_SYL=-750 mm  [stored -2.46063 ft]; LENGHT-_SYL=-742 mm  [stored -2.43438 ft]; LENGHT_CHAMFER_SYL=750 mm  [stored 2.46063 ft]; LENGHT_SYL=742 mm  [stored 2.43438 ft]; LampColourTemperature=6500 K; LampMacAdamStep=5; LampNominalLuminous=7100 lm; LuminousEfficacy=137 lm/W; Model=Resisto  1500 IP66 7100lm 865; ModelNumber=0010247; ModelReference=Resisto  1500 IP66 7100lm 865; Name=Resisto  1500 IP66 7100lm 865; NominalLength=1500 mm  [stored 4.92126 ft]; Photometric Web File=0010247.ies; PowerConsumption=52 W; PowerFactor=0.95; TypeName=Resisto  1500 IP66 7100lm 865; Weight=1.95 kg
- 0010246 RESISTO 1500 IP66 4000LM 865: Apparent Load=30 VA; BRACKET_DIST_SYL=594 mm; BRACKET_WIDTH_SYL=550 mm; Description=Resisto, integrated LED weatherproof luminaire, with UV stabilized flat diffuser designed to achieve uniform lit appearance, optimise light output and to reduce glare. 301 stainless steel diffuser clips and fixing brackets for surface mounting. Polycarbonate housing and diffuser - no yellow discolouration over time. 4000lm; 30W; 133lm/W; 6500K; SDCM<5; non dimmable; CRI80; IP66; IK08; Class I; 69,000hrs (L80B20) lifespan; 1500mm x 89mm x 88mm; D-mark.; L0650_SYL=No; L1200_SYL=No; L1500_SYL=Yes; LENGHT-_CHAMFER_SYL=-750 mm  [stored -2.46063 ft]; LENGHT-_SYL=-742 mm  [stored -2.43438 ft]; LENGHT_CHAMFER_SYL=750 mm  [stored 2.46063 ft]; LENGHT_SYL=742 mm  [stored 2.43438 ft]; LampColourTemperature=6500 K; LampMacAdamStep=5; LampNominalLuminous=4000 lm; LuminousEfficacy=133 lm/W; Model=Resisto  1500 IP66 4000lm 865; ModelNumber=0010246; ModelReference=Resisto  1500 IP66 4000lm 865; Name=Resisto  1500 IP66 4000lm 865; NominalLength=1500 mm  [stored 4.92126 ft]; Photometric Web File=0010246.ies; PowerConsumption=30 W; PowerFactor=0.95; TypeName=Resisto  1500 IP66 4000lm 865; Weight=1.87 kg
- 0010245 RESISTO 1500 IP66 8300LM 840: Apparent Load=61 VA; BRACKET_DIST_SYL=594 mm; BRACKET_WIDTH_SYL=550 mm; Description=Resisto, integrated LED weatherproof luminaire, with UV stabilized flat diffuser designed to achieve uniform lit appearance, optimise light output and to reduce glare. 301 stainless steel diffuser clips and fixing brackets for surface mounting. Polycarbonate housing and diffuser - no yellow discolouration over time. 8300lm; 61W; 136lm/W; 4000K; SDCM<5; non dimmable; CRI80; IP66; IK08; Class I; 69,000hrs (L80B20) lifespan; 1500mm x 89mm x 88mm; D-mark.; L0650_SYL=No; L1200_SYL=No; L1500_SYL=Yes; LENGHT-_CHAMFER_SYL=-750 mm  [stored -2.46063 ft]; LENGHT-_SYL=-742 mm  [stored -2.43438 ft]; LENGHT_CHAMFER_SYL=750 mm  [stored 2.46063 ft]; LENGHT_SYL=742 mm  [stored 2.43438 ft]; LampColourTemperature=4000 K; LampMacAdamStep=5; LampNominalLuminous=8300 lm; LuminousEfficacy=136 lm/W; Model=Resisto  1500 IP66 8300lm 840; ModelNumber=0010245; ModelReference=Resisto  1500 IP66 8300lm 840; Name=Resisto  1500 IP66 8300lm 840; NominalLength=1500 mm  [stored 4.92126 ft]; Photometric Web File=0010245.ies; PowerConsumption=61.0 W; PowerFactor=0.95; TypeName=Resisto  1500 IP66 8300lm 840; Weight=15.48 kg
- 0010244 RESISTO 1500 IP66 7100LM 840: Apparent Load=52 VA; BRACKET_DIST_SYL=594 mm; BRACKET_WIDTH_SYL=550 mm; Description=Resisto, integrated LED weatherproof luminaire, with UV stabilized flat diffuser designed to achieve uniform lit appearance, optimise light output and to reduce glare. 301 stainless steel diffuser clips and fixing brackets for surface mounting. Polycarbonate housing and diffuser - no yellow discolouration over time. 7100lm; 52W; 137lm/W; 4000K; SDCM<5; non dimmable; CRI80; IP66; IK08; Class I; 69,000hrs (L80B20) lifespan; 1500mm x 89mm x 88mm; D-mark.; L0650_SYL=No; L1200_SYL=No; L1500_SYL=Yes; LENGHT-_CHAMFER_SYL=-750 mm  [stored -2.46063 ft]; LENGHT-_SYL=-742 mm  [stored -2.43438 ft]; LENGHT_CHAMFER_SYL=750 mm  [stored 2.46063 ft]; LENGHT_SYL=742 mm  [stored 2.43438 ft]; LampColourTemperature=4000 K; LampMacAdamStep=5; LampNominalLuminous=7100 lm; LuminousEfficacy=137 lm/W; Model=Resisto  1500 IP66 7100lm 840; ModelNumber=0010244; ModelReference=Resisto  1500 IP66 7100lm 840; Name=Resisto  1500 IP66 7100lm 840; NominalLength=1500 mm  [stored 4.92126 ft]; Photometric Web File=0010244.ies; PowerConsumption=52.0 W; PowerFactor=0.95; TypeName=Resisto  1500 IP66 7100lm 840; Weight=15.48 kg
- 0010243 RESISTO 1500 IP66 4000LM 840: Apparent Load=30 VA; BRACKET_DIST_SYL=594 mm; BRACKET_WIDTH_SYL=550 mm; Description=Resisto, integrated LED weatherproof luminaire, with UV stabilized flat diffuser designed to achieve uniform lit appearance, optimise light output and to reduce glare. 301 stainless steel diffuser clips and fixing brackets for surface mounting. Polycarbonate housing and diffuser - no yellow discolouration over time. 4000lm; 30W; 133lm/W; 4000K; SDCM<5; non dimmable; CRI80; IP66; IK08; Class I; 69,000hrs (L80B20) lifespan; 1500mm x 89mm x 88mm; D-mark.; L0650_SYL=No; L1200_SYL=No; L1500_SYL=Yes; LENGHT-_CHAMFER_SYL=-750 mm  [stored -2.46063 ft]; LENGHT-_SYL=-742 mm  [stored -2.43438 ft]; LENGHT_CHAMFER_SYL=750 mm  [stored 2.46063 ft]; LENGHT_SYL=742 mm  [stored 2.43438 ft]; LampColourTemperature=4000 K; LampMacAdamStep=5; LampNominalLuminous=4000 lm; LuminousEfficacy=133 lm/W; Model=Resisto  1500 IP66 4000lm 840; ModelNumber=0010243; ModelReference=Resisto  1500 IP66 4000lm 840; Name=Resisto  1500 IP66 4000lm 840; NominalLength=1500 mm  [stored 4.92126 ft]; Photometric Web File=0010243.ies; PowerConsumption=30 W; PowerFactor=0.95; TypeName=Resisto  1500 IP66 4000lm 840; Weight=1.87 kg
- 0010242 RESISTO 1500 IP66 8300LM 830: Apparent Load=61 VA; BRACKET_DIST_SYL=594 mm; BRACKET_WIDTH_SYL=550 mm; Description=Resisto, integrated LED weatherproof luminaire, with UV stabilized flat diffuser designed to achieve uniform lit appearance, optimise light output and to reduce glare. 301 stainless steel diffuser clips and fixing brackets for surface mounting. Polycarbonate housing and diffuser - no yellow discolouration over time. 8300lm; 61W; 136lm/W; 3000K; SDCM<5; non dimmable; CRI80; IP66; IK08; Class I; 69,000hrs (L80B20) lifespan; 1500mm x 89mm x 88mm; D-mark.; L0650_SYL=No; L1200_SYL=No; L1500_SYL=Yes; LENGHT-_CHAMFER_SYL=-750 mm  [stored -2.46063 ft]; LENGHT-_SYL=-742 mm  [stored -2.43438 ft]; LENGHT_CHAMFER_SYL=750 mm  [stored 2.46063 ft]; LENGHT_SYL=742 mm  [stored 2.43438 ft]; LampColourTemperature=3000 K; LampMacAdamStep=5; LampNominalLuminous=8300 lm; LuminousEfficacy=136 lm/W; Model=Resisto  1500 IP66 8300lm 830; ModelNumber=0010242; ModelReference=Resisto  1500 IP66 8300lm 830; Name=Resisto  1500 IP66 8300lm 830; NominalLength=1500 mm  [stored 4.92126 ft]; Photometric Web File=0010242.ies; PowerConsumption=61 W; PowerFactor=0.95; TypeName=Resisto  1500 IP66 8300lm 830; Weight=1.95 kg
- 0010241 RESISTO 1500 IP66 7100LM 830: Apparent Load=52 VA; BRACKET_DIST_SYL=594 mm; BRACKET_WIDTH_SYL=550 mm; Description=Resisto, integrated LED weatherproof luminaire, with UV stabilized flat diffuser designed to achieve uniform lit appearance, optimise light output and to reduce glare. 301 stainless steel diffuser clips and fixing brackets for surface mounting. Polycarbonate housing and diffuser - no yellow discolouration over time. 7100lm; 52W; 137lm/W; 3000K; SDCM<5; non dimmable; CRI80; IP66; IK08; Class I; 69,000hrs (L80B20) lifespan; 1500mm x 89mm x 88mm; D-mark.; L0650_SYL=No; L1200_SYL=No; L1500_SYL=Yes; LENGHT-_CHAMFER_SYL=-750 mm  [stored -2.46063 ft]; LENGHT-_SYL=-742 mm  [stored -2.43438 ft]; LENGHT_CHAMFER_SYL=750 mm  [stored 2.46063 ft]; LENGHT_SYL=742 mm  [stored 2.43438 ft]; LampColourTemperature=3000 K; LampMacAdamStep=5; LampNominalLuminous=7100 lm; LuminousEfficacy=137 lm/W; Model=Resisto  1500 IP66 7100lm 830; ModelNumber=0010241; ModelReference=Resisto  1500 IP66 7100lm 830; Name=Resisto  1500 IP66 7100lm 830; NominalLength=1500 mm  [stored 4.92126 ft]; Photometric Web File=0010241.ies; PowerConsumption=52 W; PowerFactor=0.95; TypeName=Resisto  1500 IP66 7100lm 830; Weight=1.95 kg
- 0010240 RESISTO 1500 IP66 4000LM 830: Apparent Load=30 VA; BRACKET_DIST_SYL=594 mm; BRACKET_WIDTH_SYL=550 mm; Description=Resisto, integrated LED weatherproof luminaire, with UV stabilized flat diffuser designed to achieve uniform lit appearance, optimise light output and to reduce glare. 301 stainless steel diffuser clips and fixing brackets for surface mounting. Polycarbonate housing and diffuser - no yellow discolouration over time. 4000lm; 30W; 133lm/W; 3000K; SDCM<5; non dimmable; CRI80; IP66; IK08; Class I; 69,000hrs (L80B20) lifespan; 1500mm x 89mm x 88mm; D-mark.; L0650_SYL=No; L1200_SYL=No; L1500_SYL=Yes; LENGHT-_CHAMFER_SYL=-750 mm  [stored -2.46063 ft]; LENGHT-_SYL=-742 mm  [stored -2.43438 ft]; LENGHT_CHAMFER_SYL=750 mm  [stored 2.46063 ft]; LENGHT_SYL=742 mm  [stored 2.43438 ft]; LampColourTemperature=3000 K; LampMacAdamStep=5; LampNominalLuminous=4000 lm; LuminousEfficacy=133 lm/W; Model=Resisto  1500 IP66 4000lm 830; ModelNumber=0010240; ModelReference=Resisto  1500 IP66 4000lm 830; Name=Resisto  1500 IP66 4000lm 830; NominalLength=1500 mm  [stored 4.92126 ft]; Photometric Web File=0010240.ies; PowerConsumption=30 W; PowerFactor=0.95; TypeName=Resisto  1500 IP66 4000lm 830; Weight=1.87 kg
- 0010237 RESISTO 1200 HE IP66 DALI 4800LM 840: Apparent Load=31 VA; BRACKET_DIST_SYL=444 mm; BRACKET_WIDTH_SYL=400 mm  [stored 1.31234 ft]; Description=Resisto, integrated LED weatherproof luminaire, with UV stabilized flat diffuser designed to achieve uniform lit appearance, optimise light output and to reduce glare. 301 stainless steel diffuser clips and fixing brackets for surface mounting. Polycarbonate housing and diffuser - no yellow discolouration over time. 4800lm; 31W; 155lm/W; 4000K; SDCM<3; DALI dimmable; CRI80; IP66; IK08; Class I; 69,000hrs (L80B20) lifespan; 1200mm x 89mm x 88mm; D-mark.; L0650_SYL=No; L1200_SYL=Yes; L1500_SYL=No; LENGHT-_CHAMFER_SYL=-600 mm; LENGHT-_SYL=-592 mm  [stored -1.94226 ft]; LENGHT_CHAMFER_SYL=600 mm; LENGHT_SYL=592 mm  [stored 1.94226 ft]; LampColourTemperature=4000 K; LampMacAdamStep=3; LampNominalLuminous=4800 lm; LuminousEfficacy=155 lm/W; Model=Resisto  1200 HE IP66 DALI 4800lm 840; ModelNumber=0010237; ModelReference=Resisto  1200 HE IP66 DALI 4800lm 840; Name=Resisto  1200 HE IP66 DALI 4800lm 840; NominalLength=1200 mm; Photometric Web File=0010237.ies; PowerConsumption=31 W; PowerFactor=0.98; TypeName=Resisto  1200 HE IP66 DALI 4800lm 840; Weight=1.59 kg
- 0010236 RESISTO 1200 HE IP66 DALI 2800LM 840: Apparent Load=18 VA; BRACKET_DIST_SYL=444 mm; BRACKET_WIDTH_SYL=400 mm  [stored 1.31234 ft]; Description=Resisto, integrated LED weatherproof luminaire, with UV stabilized flat diffuser designed to achieve uniform lit appearance, optimise light output and to reduce glare. 301 stainless steel diffuser clips and fixing brackets for surface mounting. Polycarbonate housing and diffuser - no yellow discolouration over time. 2800lm; 18W; 156lm/W; 4000K; SDCM<3; DALI dimmable; CRI80; IP66; IK08; Class I; 69,000hrs (L80B20) lifespan; 1200mm x 89mm x 88mm; D-mark.; L0650_SYL=No; L1200_SYL=Yes; L1500_SYL=No; LENGHT-_CHAMFER_SYL=-600 mm; LENGHT-_SYL=-592 mm  [stored -1.94226 ft]; LENGHT_CHAMFER_SYL=600 mm; LENGHT_SYL=592 mm  [stored 1.94226 ft]; LampColourTemperature=4000 K; LampMacAdamStep=3; LampNominalLuminous=2800 lm; LuminousEfficacy=156 lm/W; Model=Resisto  1200 HE IP66 DALI 2800lm 840; ModelNumber=0010236; ModelReference=Resisto  1200 HE IP66 DALI 2800lm 840; Name=Resisto  1200 HE IP66 DALI 2800lm 840; NominalLength=1200 mm; Photometric Web File=0010236.ies; PowerConsumption=18 W; PowerFactor=0.98; TypeName=Resisto  1200 HE IP66 DALI 2800lm 840; Weight=1.51 kg
- 0010235 RESISTO 1200 HE IP66 4800LM 840 EM: Apparent Load=35 VA; BRACKET_DIST_SYL=444 mm; BRACKET_WIDTH_SYL=400 mm  [stored 1.31234 ft]; Description=Resisto, integrated LED weatherproof luminaire, with UV stabilized flat diffuser designed to achieve uniform lit appearance, optimise light output and to reduce glare. 301 stainless steel diffuser clips and fixing brackets for surface mounting. Polycarbonate housing and diffuser - no yellow discolouration over time. 4800lm; 35W; 137lm/W; 4000K; SDCM<3; non dimmable; CRI80; IP66; IK08; Class I; 69,000hrs (L80B20) lifespan; 1200mm x 89mm x 88mm; D-mark; 3-hour maintained emergency batteries.; L0650_SYL=No; L1200_SYL=Yes; L1500_SYL=No; LENGHT-_CHAMFER_SYL=-600 mm; LENGHT-_SYL=-592 mm  [stored -1.94226 ft]; LENGHT_CHAMFER_SYL=600 mm; LENGHT_SYL=592 mm  [stored 1.94226 ft]; LampColourTemperature=4000 K; LampMacAdamStep=3; LampNominalLuminous=4800 lm; LuminousEfficacy=137 lm/W; Model=Resisto  1200 HE IP66 4800lm 840 EM; ModelNumber=0010235; ModelReference=Resisto  1200 HE IP66 4800lm 840 EM; Name=Resisto  1200 HE IP66 4800lm 840 EM; NominalLength=1200 mm; Photometric Web File=0010235.ies; PowerConsumption=35 W; PowerFactor=0.95; TypeName=Resisto  1200 HE IP66 4800lm 840 EM; Weight=2.12 kg
- 0010234 RESISTO 1200 HE IP66 2800LM 840 EM: Apparent Load=22 VA; BRACKET_DIST_SYL=444 mm; BRACKET_WIDTH_SYL=400 mm  [stored 1.31234 ft]; Description=Resisto, integrated LED weatherproof luminaire, with UV stabilized flat diffuser designed to achieve uniform lit appearance, optimise light output and to reduce glare. 301 stainless steel diffuser clips and fixing brackets for surface mounting. Polycarbonate housing and diffuser - no yellow discolouration over time. 2800lm; 22W; 127lm/W; 4000K; SDCM<3; non dimmable; CRI80; IP66; IK08; Class I; 69,000hrs (L80B20) lifespan; 1200mm x 89mm x 88mm; D-mark; 3-hour maintained emergency batteries.; L0650_SYL=No; L1200_SYL=Yes; L1500_SYL=No; LENGHT-_CHAMFER_SYL=-600 mm; LENGHT-_SYL=-592 mm  [stored -1.94226 ft]; LENGHT_CHAMFER_SYL=600 mm; LENGHT_SYL=592 mm  [stored 1.94226 ft]; LampColourTemperature=4000 K; LampMacAdamStep=3; LampNominalLuminous=2800 lm; LuminousEfficacy=127 lm/W; Model=Resisto  1200 HE IP66 2800lm 840 EM; ModelNumber=0010234; ModelReference=Resisto  1200 HE IP66 2800lm 840 EM; Name=Resisto  1200 HE IP66 2800lm 840 EM; NominalLength=1200 mm; Photometric Web File=0010234.ies; PowerConsumption=22 W; PowerFactor=0.95; TypeName=Resisto  1200 HE IP66 2800lm 840 EM; Weight=2.12 kg
- 0010233 RESISTO 1200 HE IP66 4800LM 840: Apparent Load=31 VA; BRACKET_DIST_SYL=444 mm; BRACKET_WIDTH_SYL=400 mm  [stored 1.31234 ft]; Description=Resisto, integrated LED weatherproof luminaire, with UV stabilized flat diffuser designed to achieve uniform lit appearance, optimise light output and to reduce glare. 301 stainless steel diffuser clips and fixing brackets for surface mounting. Polycarbonate housing and diffuser - no yellow discolouration over time. 4800lm; 31W; 155lm/W; 4000K; SDCM<3; non dimmable; CRI80; IP66; IK08; Class I; 69,000hrs (L80B20) lifespan; 1200mm x 89mm x 88mm; D-mark.; L0650_SYL=No; L1200_SYL=Yes; L1500_SYL=No; LENGHT-_CHAMFER_SYL=-600 mm; LENGHT-_SYL=-592 mm  [stored -1.94226 ft]; LENGHT_CHAMFER_SYL=600 mm; LENGHT_SYL=592 mm  [stored 1.94226 ft]; LampColourTemperature=4000 K; LampMacAdamStep=3; LampNominalLuminous=4800 lm; LuminousEfficacy=155 lm/W; Model=Resisto  1200 HE IP66 4800lm 840; ModelNumber=0010233; ModelReference=Resisto  1200 HE IP66 4800lm 840; Name=Resisto  1200 HE IP66 4800lm 840; NominalLength=1200 mm; Photometric Web File=0010233.ies; PowerConsumption=31 W; PowerFactor=0.95; TypeName=Resisto  1200 HE IP66 4800lm 840; Weight=1.51 kg
- 0010232 RESISTO 1200 HE IP66 2800LM 840: Apparent Load=18 VA; BRACKET_DIST_SYL=444 mm; BRACKET_WIDTH_SYL=400 mm  [stored 1.31234 ft]; Description=Resisto, integrated LED weatherproof luminaire, with UV stabilized flat diffuser designed to achieve uniform lit appearance, optimise light output and to reduce glare. 301 stainless steel diffuser clips and fixing brackets for surface mounting. Polycarbonate housing and diffuser - no yellow discolouration over time. 2800lm; 18W; 156lm/W; 4000K; SDCM<3; non dimmable; CRI80; IP66; IK08; Class I; 69,000hrs (L80B20) lifespan; 1200mm x 89mm x 88mm; D-mark.; L0650_SYL=No; L1200_SYL=Yes; L1500_SYL=No; LENGHT-_CHAMFER_SYL=-600 mm; LENGHT-_SYL=-592 mm  [stored -1.94226 ft]; LENGHT_CHAMFER_SYL=600 mm; LENGHT_SYL=592 mm  [stored 1.94226 ft]; LampColourTemperature=4000 K; LampMacAdamStep=3; LampNominalLuminous=2800 lm; LuminousEfficacy=156 lm/W; Model=Resisto  1200 HE IP66 2800lm 840; ModelNumber=0010232; ModelReference=Resisto  1200 HE IP66 2800lm 840; Name=Resisto  1200 HE IP66 2800lm 840; NominalLength=1200 mm; Photometric Web File=0010232.ies; PowerConsumption=18 W; PowerFactor=0.95; TypeName=Resisto  1200 HE IP66 2800lm 840; Weight=1.5 kg
- 0010225 RESISTO 1200 IP66 DALI 4800LM 840: Apparent Load=35 VA; BRACKET_DIST_SYL=444 mm; BRACKET_WIDTH_SYL=400 mm  [stored 1.31234 ft]; Description=Resisto, integrated LED weatherproof luminaire, with UV stabilized flat diffuser designed to achieve uniform lit appearance, optimise light output and to reduce glare. 301 stainless steel diffuser clips and fixing brackets for surface mounting. Polycarbonate housing and diffuser - no yellow discolouration over time. 4800lm; 35W; 137lm/W; 4000K; SDCM<5; DALI dimmable; CRI80; IP66; IK08; Class I; 69,000hrs (L80B20) lifespan; 1200mm x 89mm x 88mm; D-mark.; L0650_SYL=No; L1200_SYL=Yes; L1500_SYL=No; LENGHT-_CHAMFER_SYL=-600 mm; LENGHT-_SYL=-592 mm  [stored -1.94226 ft]; LENGHT_CHAMFER_SYL=600 mm; LENGHT_SYL=592 mm  [stored 1.94226 ft]; LampColourTemperature=4000 K; LampMacAdamStep=5; LampNominalLuminous=4800 lm; LuminousEfficacy=137 lm/W; Model=Resisto  1200 IP66 DALI 4800lm 840; ModelNumber=0010225; ModelReference=Resisto  1200 IP66 DALI 4800lm 840; Name=Resisto  1200 IP66 DALI 4800lm 840; NominalLength=1200 mm; Photometric Web File=0010225.ies; PowerConsumption=35 W; PowerFactor=0.98; TypeName=Resisto  1200 IP66 DALI 4800lm 840; Weight=1.62 kg
- 0010224 RESISTO 1200 IP66 DALI 2800LM 840: Apparent Load=21 VA; BRACKET_DIST_SYL=444 mm; BRACKET_WIDTH_SYL=400 mm  [stored 1.31234 ft]; Description=Resisto, integrated LED weatherproof luminaire, with UV stabilized flat diffuser designed to achieve uniform lit appearance, optimise light output and to reduce glare. 301 stainless steel diffuser clips and fixing brackets for surface mounting. Polycarbonate housing and diffuser - no yellow discolouration over time. 2800lm; 21W; 133lm/W; 4000K; SDCM<5; DALI dimmable; CRI80; IP66; IK08; Class I; 69,000hrs (L80B20) lifespan; 1200mm x 89mm x 88mm; D-mark.; L0650_SYL=No; L1200_SYL=Yes; L1500_SYL=No; LENGHT-_CHAMFER_SYL=-600 mm; LENGHT-_SYL=-592 mm  [stored -1.94226 ft]; LENGHT_CHAMFER_SYL=600 mm; LENGHT_SYL=592 mm  [stored 1.94226 ft]; LampColourTemperature=4000 K; LampMacAdamStep=5; LampNominalLuminous=2800 lm; LuminousEfficacy=133 lm/W; Model=Resisto  1200 IP66 DALI 2800lm 840; ModelNumber=0010224; ModelReference=Resisto  1200 IP66 DALI 2800lm 840; Name=Resisto  1200 IP66 DALI 2800lm 840; NominalLength=1200 mm; Photometric Web File=0010224.ies; PowerConsumption=21 W; PowerFactor=0.98; TypeName=Resisto  1200 IP66 DALI 2800lm 840; Weight=1.59 kg
- 0010223 RESISTO 1200 IP66 MWCOR 4800LM 840: Apparent Load=35 VA; BRACKET_DIST_SYL=444 mm; BRACKET_WIDTH_SYL=400 mm  [stored 1.31234 ft]; Description=Resisto, integrated LED weatherproof luminaire, with UV stabilized flat diffuser designed to achieve uniform lit appearance, optimise light output and to reduce glare. 301 stainless steel diffuser clips and fixing brackets for surface mounting. Polycarbonate housing and diffuser - no yellow discolouration over time. 4800lm; 35W; 137lm/W; 4000K; SDCM<5; non dimmable; CRI80; IP66; IK08; Class I; 69,000hrs (L80B20) lifespan; 1200mm x 89mm x 88mm; D-mark; corridor function with microwave presence sensor.; L0650_SYL=No; L1200_SYL=Yes; L1500_SYL=No; LENGHT-_CHAMFER_SYL=-600 mm; LENGHT-_SYL=-592 mm  [stored -1.94226 ft]; LENGHT_CHAMFER_SYL=600 mm; LENGHT_SYL=592 mm  [stored 1.94226 ft]; LampColourTemperature=4000 K; LampMacAdamStep=5; LampNominalLuminous=4800 lm; LuminousEfficacy=137 lm/W; Model=Resisto  1200 IP66 MWcor 4800lm 840; ModelNumber=0010223; ModelReference=Resisto  1200 IP66 MWcor 4800lm 840; Name=Resisto  1200 IP66 MWcor 4800lm 840; NominalLength=1200 mm; Photometric Web File=0010223.ies; PowerConsumption=35 W; PowerFactor=0.98; TypeName=Resisto  1200 IP66 MWcor 4800lm 840; Weight=1.72 kg
- 0010222 RESISTO 1200 IP66 MWCOR 2800LM 840: Apparent Load=21 VA; BRACKET_DIST_SYL=444 mm; BRACKET_WIDTH_SYL=400 mm  [stored 1.31234 ft]; Description=Resisto, integrated LED weatherproof luminaire, with UV stabilized flat diffuser designed to achieve uniform lit appearance, optimise light output and to reduce glare. 301 stainless steel diffuser clips and fixing brackets for surface mounting. Polycarbonate housing and diffuser - no yellow discolouration over time. 2800lm; 21W; 133lm/W; 4000K; SDCM<5; non dimmable; CRI80; IP66; IK08; Class I; 69,000hrs (L80B20) lifespan; 1200mm x 89mm x 88mm; D-mark; corridor function with microwave presence sensor.; L0650_SYL=No; L1200_SYL=Yes; L1500_SYL=No; LENGHT-_CHAMFER_SYL=-600 mm; LENGHT-_SYL=-592 mm  [stored -1.94226 ft]; LENGHT_CHAMFER_SYL=600 mm; LENGHT_SYL=592 mm  [stored 1.94226 ft]; LampColourTemperature=4000 K; LampMacAdamStep=5; LampNominalLuminous=2800 lm; LuminousEfficacy=133 lm/W; Model=Resisto  1200 IP66 MWcor 2800lm 840; ModelNumber=0010222; ModelReference=Resisto  1200 IP66 MWcor 2800lm 840; Name=Resisto  1200 IP66 MWcor 2800lm 840; NominalLength=1200 mm; Photometric Web File=0010222.ies; PowerConsumption=21 W; PowerFactor=0.98; TypeName=Resisto  1200 IP66 MWcor 2800lm 840; Weight=1.64 kg
- 0010221 RESISTO 1200 IP66 MW 4800LM 840: Apparent Load=35 VA; BRACKET_DIST_SYL=444 mm; BRACKET_WIDTH_SYL=400 mm  [stored 1.31234 ft]; Description=Resisto, integrated LED weatherproof luminaire, with UV stabilized flat diffuser designed to achieve uniform lit appearance, optimise light output and to reduce glare. 301 stainless steel diffuser clips and fixing brackets for surface mounting. Polycarbonate housing and diffuser - no yellow discolouration over time. 4800lm; 35W; 137lm/W; 4000K; SDCM<5; non dimmable; CRI80; IP66; IK08; Class I; 69,000hrs (L80B20) lifespan; 1200mm x 89mm x 88mm; D-mark; MW On/Off.; L0650_SYL=No; L1200_SYL=Yes; L1500_SYL=No; LENGHT-_CHAMFER_SYL=-600 mm; LENGHT-_SYL=-592 mm  [stored -1.94226 ft]; LENGHT_CHAMFER_SYL=600 mm; LENGHT_SYL=592 mm  [stored 1.94226 ft]; LampColourTemperature=4000 K; LampMacAdamStep=5; LampNominalLuminous=4800 lm; LuminousEfficacy=137 lm/W; Model=Resisto  1200 IP66 MW 4800lm 840; ModelNumber=0010221; ModelReference=Resisto  1200 IP66 MW 4800lm 840; Name=Resisto  1200 IP66 MW 4800lm 840; NominalLength=1200 mm; Photometric Web File=0010221.ies; PowerConsumption=35 W; PowerFactor=0.95; TypeName=Resisto  1200 IP66 MW 4800lm 840; Weight=1.59 kg
- 0010220 RESISTO 1200 IP66 MW 2800LM 840: Apparent Load=21 VA; BRACKET_DIST_SYL=444 mm; BRACKET_WIDTH_SYL=400 mm  [stored 1.31234 ft]; Description=Resisto, integrated LED weatherproof luminaire, with UV stabilized flat diffuser designed to achieve uniform lit appearance, optimise light output and to reduce glare. 301 stainless steel diffuser clips and fixing brackets for surface mounting. Polycarbonate housing and diffuser - no yellow discolouration over time. 2800lm; 21W; 133lm/W; 4000K; SDCM<5; non dimmable; CRI80; IP66; IK08; Class I; 69,000hrs (L80B20) lifespan; 1200mm x 89mm x 88mm; D-mark; MW On/Off.; L0650_SYL=No; L1200_SYL=Yes; L1500_SYL=No; LENGHT-_CHAMFER_SYL=-600 mm; LENGHT-_SYL=-592 mm  [stored -1.94226 ft]; LENGHT_CHAMFER_SYL=600 mm; LENGHT_SYL=592 mm  [stored 1.94226 ft]; LampColourTemperature=4000 K; LampMacAdamStep=5; LampNominalLuminous=2800 lm; LuminousEfficacy=133 lm/W; Model=Resisto  1200 IP66 MW 2800lm 840; ModelNumber=0010220; ModelReference=Resisto  1200 IP66 MW 2800lm 840; Name=Resisto  1200 IP66 MW 2800lm 840; NominalLength=1200 mm; Photometric Web File=0010220.ies; PowerConsumption=21 W; PowerFactor=0.95; TypeName=Resisto  1200 IP66 MW 2800lm 840; Weight=1.55 kg
- 0010219 RESISTO 1200 IP66 4800LM 840 EM: Apparent Load=39 VA; BRACKET_DIST_SYL=444 mm; BRACKET_WIDTH_SYL=400 mm  [stored 1.31234 ft]; Description=Resisto, integrated LED weatherproof luminaire, with UV stabilized flat diffuser designed to achieve uniform lit appearance, optimise light output and to reduce glare. 301 stainless steel diffuser clips and fixing brackets for surface mounting. Polycarbonate housing and diffuser - no yellow discolouration over time. 4800lm; 39W; 123lm/W; 4000K; SDCM<5; non dimmable; CRI80; IP66; IK08; Class I; 69,000hrs (L80B20) lifespan; 1200mm x 89mm x 88mm; D-mark; 3-hour maintained emergency batteries.; L0650_SYL=No; L1200_SYL=Yes; L1500_SYL=No; LENGHT-_CHAMFER_SYL=-600 mm; LENGHT-_SYL=-592 mm  [stored -1.94226 ft]; LENGHT_CHAMFER_SYL=600 mm; LENGHT_SYL=592 mm  [stored 1.94226 ft]; LampColourTemperature=4000 K; LampMacAdamStep=5; LampNominalLuminous=4800 lm; LuminousEfficacy=123 lm/W; Model=Resisto  1200 IP66 4800lm 840 EM; ModelNumber=0010219; ModelReference=Resisto  1200 IP66 4800lm 840 EM; Name=Resisto  1200 IP66 4800lm 840 EM; NominalLength=1200 mm; Photometric Web File=0010219.ies; PowerConsumption=39 W; PowerFactor=0.95; TypeName=Resisto  1200 IP66 4800lm 840 EM; Weight=2.16 kg
- 0010218 RESISTO 1200 IP66 2800LM 840 EM: Apparent Load=25 VA; BRACKET_DIST_SYL=444 mm; BRACKET_WIDTH_SYL=400 mm  [stored 1.31234 ft]; Description=Resisto, integrated LED weatherproof luminaire, with UV stabilized flat diffuser designed to achieve uniform lit appearance, optimise light output and to reduce glare. 301 stainless steel diffuser clips and fixing brackets for surface mounting. Polycarbonate housing and diffuser - no yellow discolouration over time. 2800lm; 25W; 112lm/W; 4000K; SDCM<5; non dimmable; CRI80; IP66; IK08; Class I; 69,000hrs (L80B20) lifespan; 1200mm x 89mm x 88mm; D-mark; 3-hour maintained emergency batteries.; L0650_SYL=No; L1200_SYL=Yes; L1500_SYL=No; LENGHT-_CHAMFER_SYL=-600 mm; LENGHT-_SYL=-592 mm  [stored -1.94226 ft]; LENGHT_CHAMFER_SYL=600 mm; LENGHT_SYL=592 mm  [stored 1.94226 ft]; LampColourTemperature=4000 K; LampMacAdamStep=5; LampNominalLuminous=2800 lm; LuminousEfficacy=112 lm/W; Model=Resisto  1200 IP66 2800lm 840 EM; ModelNumber=0010218; ModelReference=Resisto  1200 IP66 2800lm 840 EM; Name=Resisto  1200 IP66 2800lm 840 EM; NominalLength=1200 mm; Photometric Web File=0010218.ies; PowerConsumption=25 W; PowerFactor=0.95; TypeName=Resisto  1200 IP66 2800lm 840 EM; Weight=2.12 kg
- 0010217 RESISTO 1200 IP66 4800LM 840 5XTH: Apparent Load=35 VA; BRACKET_DIST_SYL=444 mm; BRACKET_WIDTH_SYL=400 mm  [stored 1.31234 ft]; Description=Resisto, integrated LED weatherproof luminaire, with UV stabilized flat diffuser designed to achieve uniform lit appearance, optimise light output and to reduce glare. 301 stainless steel diffuser clips and fixing brackets for surface mounting. Polycarbonate housing and diffuser - no yellow discolouration over time. 4800lm; 35W; 137lm/W; 4000K; SDCM<5; non dimmable; CRI80; IP66; IK08; Class I; 69,000hrs (L80B20) lifespan; 1200mm x 89mm x 88mm; D-mark; through wiring.; L0650_SYL=No; L1200_SYL=Yes; L1500_SYL=No; LENGHT-_CHAMFER_SYL=-600 mm; LENGHT-_SYL=-592 mm  [stored -1.94226 ft]; LENGHT_CHAMFER_SYL=600 mm; LENGHT_SYL=592 mm  [stored 1.94226 ft]; LampColourTemperature=4000 K; LampMacAdamStep=5; LampNominalLuminous=4800 lm; LuminousEfficacy=137 lm/W; Model=Resisto 1200 IP66 4800lm 840 5xTH; ModelNumber=0010217; ModelReference=Resisto 1200 IP66 4800lm 840 5xTH; Name=Resisto 1200 IP66 4800lm 840 5xTH; NominalLength=1200 mm; Photometric Web File=0010217.ies; PowerConsumption=35 W; PowerFactor=0.95; TypeName=Resisto 1200 IP66 4800lm 840 5xTH; Weight=1.72 kg
- 0010216 RESISTO 1200 IP66 2800LM 840 5XTH: Apparent Load=21 VA; BRACKET_DIST_SYL=444 mm; BRACKET_WIDTH_SYL=400 mm  [stored 1.31234 ft]; Description=Resisto, integrated LED weatherproof luminaire, with UV stabilized flat diffuser designed to achieve uniform lit appearance, optimise light output and to reduce glare. 301 stainless steel diffuser clips and fixing brackets for surface mounting. Polycarbonate housing and diffuser - no yellow discolouration over time. 2800lm; 21W; 133lm/W; 4000K; SDCM<5; non dimmable; CRI80; IP66; IK08; Class I; 69,000hrs (L80B20) lifespan; 1200mm x 89mm x 88mm; D-mark; through wiring.; L0650_SYL=No; L1200_SYL=Yes; L1500_SYL=No; LENGHT-_CHAMFER_SYL=-600 mm; LENGHT-_SYL=-592 mm  [stored -1.94226 ft]; LENGHT_CHAMFER_SYL=600 mm; LENGHT_SYL=592 mm  [stored 1.94226 ft]; LampColourTemperature=4000 K; LampMacAdamStep=5; LampNominalLuminous=2800 lm; LuminousEfficacy=133 lm/W; Model=Resisto 1200 IP66 2800lm 840 5xTH; ModelNumber=0010216; ModelReference=Resisto 1200 IP66 2800lm 840 5xTH; Name=Resisto 1200 IP66 2800lm 840 5xTH; NominalLength=1200 mm; Photometric Web File=0010216.ies; PowerConsumption=21 W; PowerFactor=0.95; TypeName=Resisto 1200 IP66 2800lm 840 5xTH; Weight=1.68 kg
- 0010215 RESISTO 1200 IP66 4800LM 840 QC: Apparent Load=35 VA; BRACKET_DIST_SYL=444 mm; BRACKET_WIDTH_SYL=400 mm  [stored 1.31234 ft]; Description=Resisto, integrated LED weatherproof luminaire, with UV stabilized flat diffuser designed to achieve uniform lit appearance, optimise light output and to reduce glare. 301 stainless steel diffuser clips and fixing brackets for surface mounting. Polycarbonate housing and diffuser - no yellow discolouration over time. 4800lm; 35W; 137lm/W; 4000K; SDCM<5; non dimmable; CRI80; IP66; IK08; Class I; 69,000hrs (L80B20) lifespan; 1200mm x 89mm x 88mm; D-mark; assembled with quick connector.; L0650_SYL=No; L1200_SYL=Yes; L1500_SYL=No; LENGHT-_CHAMFER_SYL=-600 mm; LENGHT-_SYL=-592 mm  [stored -1.94226 ft]; LENGHT_CHAMFER_SYL=600 mm; LENGHT_SYL=592 mm  [stored 1.94226 ft]; LampColourTemperature=4000 K; LampMacAdamStep=5; LampNominalLuminous=4800 lm; LuminousEfficacy=137 lm/W; Model=Resisto  1200 IP66 4800lm 840 QC; ModelNumber=0010215; ModelReference=Resisto  1200 IP66 4800lm 840 QC; Name=Resisto  1200 IP66 4800lm 840 QC; NominalLength=1212 mm  [stored 3.97638 ft]; Photometric Web File=0010215.ies; PowerConsumption=35 W; PowerFactor=0.95; TypeName=Resisto  1200 IP66 4800lm 840 QC; Weight=1.61 kg
- 0010214 RESISTO 1200 IP66 2800LM 840 QC: Apparent Load=21 VA; BRACKET_DIST_SYL=444 mm; BRACKET_WIDTH_SYL=400 mm  [stored 1.31234 ft]; Description=Resisto, integrated LED weatherproof luminaire, with UV stabilized flat diffuser designed to achieve uniform lit appearance, optimise light output and to reduce glare. 301 stainless steel diffuser clips and fixing brackets for surface mounting. Polycarbonate housing and diffuser - no yellow discolouration over time. 2800lm; 21W; 133lm/W; 4000K; SDCM<5; non dimmable; CRI80; IP66; IK08; Class I; 69,000hrs (L80B20) lifespan; 1200mm x 89mm x 88mm; D-mark; assembled with quick connector.; L0650_SYL=No; L1200_SYL=Yes; L1500_SYL=No; LENGHT-_CHAMFER_SYL=-600 mm; LENGHT-_SYL=-592 mm  [stored -1.94226 ft]; LENGHT_CHAMFER_SYL=600 mm; LENGHT_SYL=592 mm  [stored 1.94226 ft]; LampColourTemperature=4000 K; LampMacAdamStep=5; LampNominalLuminous=2800 lm; LuminousEfficacy=133 lm/W; Model=Resisto  1200 IP66 2800lm 840 QC; ModelNumber=0010214; ModelReference=Resisto  1200 IP66 2800lm 840 QC; Name=Resisto  1200 IP66 2800lm 840 QC; NominalLength=1212 mm  [stored 3.97638 ft]; Photometric Web File=0010214.ies; PowerConsumption=21 W; PowerFactor=0.95; TypeName=Resisto  1200 IP66 2800lm 840 QC; Weight=1.57 kg
- 0010213 RESISTO 1200 IP66 4800LM 865: Apparent Load=35 VA; BRACKET_DIST_SYL=444 mm; BRACKET_WIDTH_SYL=400 mm  [stored 1.31234 ft]; Description=Resisto, integrated LED weatherproof luminaire, with UV stabilized flat diffuser designed to achieve uniform lit appearance, optimise light output and to reduce glare. 301 stainless steel diffuser clips and fixing brackets for surface mounting. Polycarbonate housing and diffuser - no yellow discolouration over time. 4800lm; 35W; 137lm/W; 6500K; SDCM<5; non dimmable; CRI80; IP66; IK08; Class I; 69,000hrs (L80B20) lifespan; 1200mm x 89mm x 88mm; D-mark.; L0650_SYL=No; L1200_SYL=Yes; L1500_SYL=No; LENGHT-_CHAMFER_SYL=-600 mm; LENGHT-_SYL=-592 mm  [stored -1.94226 ft]; LENGHT_CHAMFER_SYL=600 mm; LENGHT_SYL=592 mm  [stored 1.94226 ft]; LampColourTemperature=6500 K; LampMacAdamStep=5; LampNominalLuminous=4800 lm; LuminousEfficacy=137 lm/W; Model=Resisto  1200 IP66 4800lm 865; ModelNumber=0010213; ModelReference=Resisto  1200 IP66 4800lm 865; Name=Resisto  1200 IP66 4800lm 865; NominalLength=1200 mm; Photometric Web File=0010213.ies; PowerConsumption=35 W; PowerFactor=0.95; TypeName=Resisto  1200 IP66 4800lm 865; Weight=1.54 kg
- 0010212 RESISTO 1200 IP66 2800LM 865: Apparent Load=21 VA; BRACKET_DIST_SYL=444 mm; BRACKET_WIDTH_SYL=400 mm  [stored 1.31234 ft]; Description=Resisto, integrated LED weatherproof luminaire, with UV stabilized flat diffuser designed to achieve uniform lit appearance, optimise light output and to reduce glare. 301 stainless steel diffuser clips and fixing brackets for surface mounting. Polycarbonate housing and diffuser - no yellow discolouration over time. 2800lm; 21W; 133lm/W; 6500K; SDCM<5; non dimmable; CRI80; IP66; IK08; Class I; 69,000hrs (L80B20) lifespan; 1200mm x 89mm x 88mm; D-mark.; L0650_SYL=No; L1200_SYL=Yes; L1500_SYL=No; LENGHT-_CHAMFER_SYL=-600 mm; LENGHT-_SYL=-592 mm  [stored -1.94226 ft]; LENGHT_CHAMFER_SYL=600 mm; LENGHT_SYL=592 mm  [stored 1.94226 ft]; LampColourTemperature=6500 K; LampMacAdamStep=5; LampNominalLuminous=2800 lm; LuminousEfficacy=133 lm/W; Model=Resisto  1200 IP66 2800lm 865; ModelNumber=0010212; ModelReference=Resisto  1200 IP66 2800lm 865; Name=Resisto  1200 IP66 2800lm 865; NominalLength=1200 mm; Photometric Web File=0010212.ies; PowerConsumption=21 W; PowerFactor=0.95; TypeName=Resisto  1200 IP66 2800lm 865; Weight=1.5 kg
- 0010211 RESISTO 1200 IP66 4800LM 840: Apparent Load=35 VA; BRACKET_DIST_SYL=444 mm; BRACKET_WIDTH_SYL=400 mm  [stored 1.31234 ft]; Description=Resisto, integrated LED weatherproof luminaire, with UV stabilized flat diffuser designed to achieve uniform lit appearance, optimise light output and to reduce glare. 301 stainless steel diffuser clips and fixing brackets for surface mounting. Polycarbonate housing and diffuser - no yellow discolouration over time. 4800lm; 35W; 137lm/W; 4000K; SDCM<5; non dimmable; CRI80; IP66; IK08; Class I; 69,000hrs (L80B20) lifespan; 1200mm x 89mm x 88mm; D-mark.; L0650_SYL=No; L1200_SYL=Yes; L1500_SYL=No; LENGHT-_CHAMFER_SYL=-600 mm; LENGHT-_SYL=-592 mm  [stored -1.94226 ft]; LENGHT_CHAMFER_SYL=600 mm; LENGHT_SYL=592 mm  [stored 1.94226 ft]; LampColourTemperature=4000 K; LampMacAdamStep=5; LampNominalLuminous=4800 lm; LuminousEfficacy=137 lm/W; Model=Resisto  1200 IP66 4800lm 840; ModelNumber=0010211; ModelReference=Resisto  1200 IP66 4800lm 840; Name=Resisto  1200 IP66 4800lm 840; NominalLength=1200 mm; Photometric Web File=0010211.ies; PowerConsumption=35.0 W; PowerFactor=0.95; TypeName=Resisto  1200 IP66 4800lm 840; Weight=11.88 kg
- 0010210 RESISTO 1200 IP66 2800LM 840: Apparent Load=21 VA; BRACKET_DIST_SYL=444 mm; BRACKET_WIDTH_SYL=400 mm  [stored 1.31234 ft]; Description=Resisto, integrated LED weatherproof luminaire, with UV stabilized flat diffuser designed to achieve uniform lit appearance, optimise light output and to reduce glare. 301 stainless steel diffuser clips and fixing brackets for surface mounting. Polycarbonate housing and diffuser - no yellow discolouration over time. 2800lm; 21W; 133lm/W; 4000K; SDCM<5; non dimmable; CRI80; IP66; IK08; Class I; 69,000hrs (L80B20) lifespan; 1200mm x 89mm x 88mm; D-mark.; L0650_SYL=No; L1200_SYL=Yes; L1500_SYL=No; LENGHT-_CHAMFER_SYL=-600 mm; LENGHT-_SYL=-592 mm  [stored -1.94226 ft]; LENGHT_CHAMFER_SYL=600 mm; LENGHT_SYL=592 mm  [stored 1.94226 ft]; LampColourTemperature=4000 K; LampMacAdamStep=5; LampNominalLuminous=2800 lm; LuminousEfficacy=133 lm/W; Model=Resisto  1200 IP66 2800lm 840; ModelNumber=0010210; ModelReference=Resisto  1200 IP66 2800lm 840; Name=Resisto  1200 IP66 2800lm 840; NominalLength=1200 mm; Photometric Web File=0010210.ies; PowerConsumption=21.0 W; PowerFactor=0.95; TypeName=Resisto  1200 IP66 2800lm 840; Weight=11.88 kg
- 0010209 RESISTO 1200 IP66 4800LM 830: Apparent Load=35 VA; BRACKET_DIST_SYL=444 mm; BRACKET_WIDTH_SYL=400 mm  [stored 1.31234 ft]; Description=Resisto, integrated LED weatherproof luminaire, with UV stabilized flat diffuser designed to achieve uniform lit appearance, optimise light output and to reduce glare. 301 stainless steel diffuser clips and fixing brackets for surface mounting. Polycarbonate housing and diffuser - no yellow discolouration over time. 4800lm; 35W; 137lm/W; 3000K; SDCM<5; non dimmable; CRI80; IP66; IK08; Class I; 69,000hrs (L80B20) lifespan; 1200mm x 89mm x 88mm; D-mark.; L0650_SYL=No; L1200_SYL=Yes; L1500_SYL=No; LENGHT-_CHAMFER_SYL=-600 mm; LENGHT-_SYL=-592 mm  [stored -1.94226 ft]; LENGHT_CHAMFER_SYL=600 mm; LENGHT_SYL=592 mm  [stored 1.94226 ft]; LampColourTemperature=3000 K; LampMacAdamStep=5; LampNominalLuminous=4800 lm; LuminousEfficacy=137 lm/W; Model=Resisto  1200 IP66 4800lm 830; ModelNumber=0010209; ModelReference=Resisto  1200 IP66 4800lm 830; Name=Resisto  1200 IP66 4800lm 830; NominalLength=1200 mm; Photometric Web File=0010209.ies; PowerConsumption=35 W; PowerFactor=0.95; TypeName=Resisto  1200 IP66 4800lm 830; Weight=1.54 kg
- 0010208 RESISTO 1200 IP66 2800LM 830: Apparent Load=21 VA; BRACKET_DIST_SYL=444 mm; BRACKET_WIDTH_SYL=400 mm  [stored 1.31234 ft]; Description=Resisto, integrated LED weatherproof luminaire, with UV stabilized flat diffuser designed to achieve uniform lit appearance, optimise light output and to reduce glare. 301 stainless steel diffuser clips and fixing brackets for surface mounting. Polycarbonate housing and diffuser - no yellow discolouration over time. 2800lm; 21W; 133lm/W; 3000K; SDCM<5; non dimmable; CRI80; IP66; IK08; Class I; 69,000hrs (L80B20) lifespan; 1200mm x 89mm x 88mm; D-mark.; L0650_SYL=No; L1200_SYL=Yes; L1500_SYL=No; LENGHT-_CHAMFER_SYL=-600 mm; LENGHT-_SYL=-592 mm  [stored -1.94226 ft]; LENGHT_CHAMFER_SYL=600 mm; LENGHT_SYL=592 mm  [stored 1.94226 ft]; LampColourTemperature=3000 K; LampMacAdamStep=5; LampNominalLuminous=2800 lm; LuminousEfficacy=133 lm/W; Model=Resisto  1200 IP66 2800lm 830; ModelNumber=0010208; ModelReference=Resisto  1200 IP66 2800lm 830; Name=Resisto  1200 IP66 2800lm 830; NominalLength=1200 mm; Photometric Web File=0010208.ies; PowerConsumption=21 W; PowerFactor=0.95; TypeName=Resisto  1200 IP66 2800lm 830; Weight=1.5 kg
- 0010207 RESISTO 600 HE IP66 2500LM 840: Apparent Load=16 VA; BRACKET_DIST_SYL=169 mm; BRACKET_WIDTH_SYL=125 mm; Description=Resisto, integrated LED weatherproof luminaire, with UV stabilized flat diffuser designed to achieve uniform lit appearance, optimise light output and to reduce glare. 301 stainless steel diffuser clips and fixing brackets for surface mounting. Polycarbonate housing and diffuser - no yellow discolouration over time. 2500lm; 16W; 156lm/W; 4000K; SDCM<3; non dimmable; CRI80; IP66; IK08; Class I; 69,000hrs (L80B20) lifespan; 650mm x 89mm x 88mm; D-mark.; L0650_SYL=Yes; L1200_SYL=No; L1500_SYL=No; LENGHT-_CHAMFER_SYL=-325 mm  [stored -1.06627 ft]; LENGHT-_SYL=-317 mm  [stored -1.04003 ft]; LENGHT_CHAMFER_SYL=325 mm  [stored 1.06627 ft]; LENGHT_SYL=317 mm  [stored 1.04003 ft]; LampColourTemperature=4000 K; LampMacAdamStep=3; LampNominalLuminous=2500 lm; LuminousEfficacy=156 lm/W; Model=Resisto  600 HE IP66 2500lm 840; ModelNumber=0010207; ModelReference=Resisto  600 HE IP66 2500lm 840; Name=Resisto  600 HE IP66 2500lm 840; NominalLength=650 mm  [stored 2.13255 ft]; Photometric Web File=0010207.ies; PowerConsumption=16 W; PowerFactor=0.95; TypeName=Resisto  600 HE IP66 2500lm 840; Weight=0.96 kg
- 0010206 RESISTO 600 HE IP66 1400LM 840: Apparent Load=10 VA; BRACKET_DIST_SYL=169 mm; BRACKET_WIDTH_SYL=125 mm; Description=Resisto, integrated LED weatherproof luminaire, with UV stabilized flat diffuser designed to achieve uniform lit appearance, optimise light output and to reduce glare. 301 stainless steel diffuser clips and fixing brackets for surface mounting. Polycarbonate housing and diffuser - no yellow discolouration over time. 1400lm; 10W; 140lm/W; 4000K; SDCM<3; non dimmable; CRI80; IP66; IK08; Class I; 69,000hrs (L80B20) lifespan; 650mm x 89mm x 88mm; D-mark.; L0650_SYL=Yes; L1200_SYL=No; L1500_SYL=No; LENGHT-_CHAMFER_SYL=-325 mm  [stored -1.06627 ft]; LENGHT-_SYL=-317 mm  [stored -1.04003 ft]; LENGHT_CHAMFER_SYL=325 mm  [stored 1.06627 ft]; LENGHT_SYL=317 mm  [stored 1.04003 ft]; LampColourTemperature=4000 K; LampMacAdamStep=3; LampNominalLuminous=1400 lm; LuminousEfficacy=140 lm/W; Model=Resisto  600 HE IP66 1400lm 840; ModelNumber=0010206; ModelReference=Resisto  600 HE IP66 1400lm 840; Name=Resisto  600 HE IP66 1400lm 840; NominalLength=650 mm  [stored 2.13255 ft]; Photometric Web File=0010206.ies; PowerConsumption=10 W; PowerFactor=0.9; TypeName=Resisto  600 HE IP66 1400lm 840; Weight=0.88 kg
- 0010205 RESISTO 600 IP66 2500LM 865: Apparent Load=19 VA; BRACKET_DIST_SYL=169 mm; BRACKET_WIDTH_SYL=125 mm; Description=Resisto, integrated LED weatherproof luminaire, with UV stabilized flat diffuser designed to achieve uniform lit appearance, optimise light output and to reduce glare. 301 stainless steel diffuser clips and fixing brackets for surface mounting. Polycarbonate housing and diffuser - no yellow discolouration over time. 2500lm; 19W; 132lm/W; 6500K; SDCM<5; non dimmable; CRI80; IP66; IK08; Class I; 69,000hrs (L80B20) lifespan; 650mm x 89mm x 88mm; D-mark.; L0650_SYL=Yes; L1200_SYL=No; L1500_SYL=No; LENGHT-_CHAMFER_SYL=-325 mm  [stored -1.06627 ft]; LENGHT-_SYL=-317 mm  [stored -1.04003 ft]; LENGHT_CHAMFER_SYL=325 mm  [stored 1.06627 ft]; LENGHT_SYL=317 mm  [stored 1.04003 ft]; LampColourTemperature=6500 K; LampMacAdamStep=5; LampNominalLuminous=2500 lm; LuminousEfficacy=132 lm/W; Model=Resisto  600 IP66 2500lm 865; ModelNumber=0010205; ModelReference=Resisto  600 IP66 2500lm 865; Name=Resisto  600 IP66 2500lm 865; NominalLength=650 mm  [stored 2.13255 ft]; Photometric Web File=0010205.ies; PowerConsumption=19 W; PowerFactor=1; TypeName=Resisto  600 IP66 2500lm 865; Weight=0.88 kg
- 0010204 RESISTO 600 IP66 1600LM 865: Apparent Load=12 VA; BRACKET_DIST_SYL=169 mm; BRACKET_WIDTH_SYL=125 mm; Description=Resisto, integrated LED weatherproof luminaire, with UV stabilized flat diffuser designed to achieve uniform lit appearance, optimise light output and to reduce glare. 301 stainless steel diffuser clips and fixing brackets for surface mounting. Polycarbonate housing and diffuser - no yellow discolouration over time. 1600lm; 12W; 133lm/W; 6500K; SDCM<5; non dimmable; CRI80; IP66; IK08; Class I; 69,000hrs (L80B20) lifespan; 650mm x 89mm x 88mm; D-mark.; L0650_SYL=Yes; L1200_SYL=No; L1500_SYL=No; LENGHT-_CHAMFER_SYL=-325 mm  [stored -1.06627 ft]; LENGHT-_SYL=-317 mm  [stored -1.04003 ft]; LENGHT_CHAMFER_SYL=325 mm  [stored 1.06627 ft]; LENGHT_SYL=317 mm  [stored 1.04003 ft]; LampColourTemperature=6500 K; LampMacAdamStep=5; LampNominalLuminous=1600 lm; LuminousEfficacy=133 lm/W; Model=Resisto  600 IP66 1600lm 865; ModelNumber=0010204; ModelReference=Resisto  600 IP66 1600lm 865; Name=Resisto  600 IP66 1600lm 865; NominalLength=650 mm  [stored 2.13255 ft]; Photometric Web File=0010204.ies; PowerConsumption=12 W; PowerFactor=0.9; TypeName=Resisto  600 IP66 1600lm 865; Weight=0.88 kg
- 0010203 RESISTO 600 IP66 2500LM 840: Apparent Load=19 VA; BRACKET_DIST_SYL=169 mm; BRACKET_WIDTH_SYL=125 mm; Description=Resisto, integrated LED weatherproof luminaire, with UV stabilized flat diffuser designed to achieve uniform lit appearance, optimise light output and to reduce glare. 301 stainless steel diffuser clips and fixing brackets for surface mounting. Polycarbonate housing and diffuser - no yellow discolouration over time. 2500lm; 19W; 132lm/W; 4000K; SDCM<5; non dimmable; CRI80; IP66; IK08; Class I; 69,000hrs (L80B20) lifespan; 650mm x 89mm x 88mm; D-mark.; L0650_SYL=Yes; L1200_SYL=No; L1500_SYL=No; LENGHT-_CHAMFER_SYL=-325 mm  [stored -1.06627 ft]; LENGHT-_SYL=-317 mm  [stored -1.04003 ft]; LENGHT_CHAMFER_SYL=325 mm  [stored 1.06627 ft]; LENGHT_SYL=317 mm  [stored 1.04003 ft]; LampColourTemperature=4000 K; LampMacAdamStep=5; LampNominalLuminous=2500 lm; LuminousEfficacy=132 lm/W; Model=Resisto  600 IP66 2500lm 840; ModelNumber=0010203; ModelReference=Resisto  600 IP66 2500lm 840; Name=Resisto  600 IP66 2500lm 840; NominalLength=650 mm  [stored 2.13255 ft]; Photometric Web File=0010203.ies; PowerConsumption=19.0 W; PowerFactor=0.95; TypeName=Resisto  600 IP66 2500lm 840; Weight=10.2 kg
- 0010202 RESISTO 600 IP66 1600LM 840: Apparent Load=12 VA; BRACKET_DIST_SYL=169 mm; BRACKET_WIDTH_SYL=125 mm; Description=Resisto, integrated LED weatherproof luminaire, with UV stabilized flat diffuser designed to achieve uniform lit appearance, optimise light output and to reduce glare. 301 stainless steel diffuser clips and fixing brackets for surface mounting. Polycarbonate housing and diffuser - no yellow discolouration over time. 1600lm; 12W; 133lm/W; 4000K; SDCM<5; non dimmable; CRI80; IP66; IK08; Class I; 69,000hrs (L80B20) lifespan; 650mm x 89mm x 88mm; D-mark.; L0650_SYL=Yes; L1200_SYL=No; L1500_SYL=No; LENGHT-_CHAMFER_SYL=-325 mm  [stored -1.06627 ft]; LENGHT-_SYL=-317 mm  [stored -1.04003 ft]; LENGHT_CHAMFER_SYL=325 mm  [stored 1.06627 ft]; LENGHT_SYL=317 mm  [stored 1.04003 ft]; LampColourTemperature=4000 K; LampMacAdamStep=5; LampNominalLuminous=1600 lm; LuminousEfficacy=133 lm/W; Model=Resisto  600 IP66 1600lm 840; ModelNumber=0010202; ModelReference=Resisto  600 IP66 1600lm 840; Name=Resisto  600 IP66 1600lm 840; NominalLength=650 mm  [stored 2.13255 ft]; Photometric Web File=0010202.ies; PowerConsumption=12.0 W; PowerFactor=0.9; TypeName=Resisto  600 IP66 1600lm 840; Weight=10.2 kg
- 0010279 RESISTO 1500 HE IP66 DALI 8300LM 840: Apparent Load=54 VA; BRACKET_DIST_SYL=594 mm; BRACKET_WIDTH_SYL=550 mm; Description=Resisto, integrated LED weatherproof luminaire, with UV stabilized flat diffuser designed to achieve uniform lit appearance, optimise light output and to reduce glare. 301 stainless steel diffuser clips and fixing brackets for surface mounting. Polycarbonate housing and diffuser - no yellow discolouration over time. 8300lm; 54W; 154lm/W; 4000K; SDCM<3; DALI dimmable; CRI80; IP66; IK08; Class I; 69,000hrs (L80B20) lifespan; 1500mm x 89mm x 88mm; D-mark.; L0650_SYL=No; L1200_SYL=No; L1500_SYL=Yes; LENGHT-_CHAMFER_SYL=-750 mm  [stored -2.46063 ft]; LENGHT-_SYL=-742 mm  [stored -2.43438 ft]; LENGHT_CHAMFER_SYL=750 mm  [stored 2.46063 ft]; LENGHT_SYL=742 mm  [stored 2.43438 ft]; LampColourTemperature=4000 K; LampMacAdamStep=3; LampNominalLuminous=8300 lm; LuminousEfficacy=154 lm/W; Model=Resisto 1500 HE IP66 DALI 8300lm 840; ModelNumber=0010279; ModelReference=Resisto 1500 HE IP66 DALI 8300lm 840; Name=Resisto 1500 HE IP66 DALI 8300lm 840; NominalLength=1500 mm  [stored 4.92126 ft]; Photometric Web File=0010279.ies; PowerConsumption=54 W; PowerFactor=0.99; TypeName=Resisto 1500 HE IP66 DALI 8300lm 840; Weight=2.01 kg

note: [stored X ft] marks values corroborated as IEEE doubles in the binary element streams (Revit-internal decimal feet)

## geometry (parser evidence)
native form markers: Sweep x3
no freeform markers — native parametric forms only
